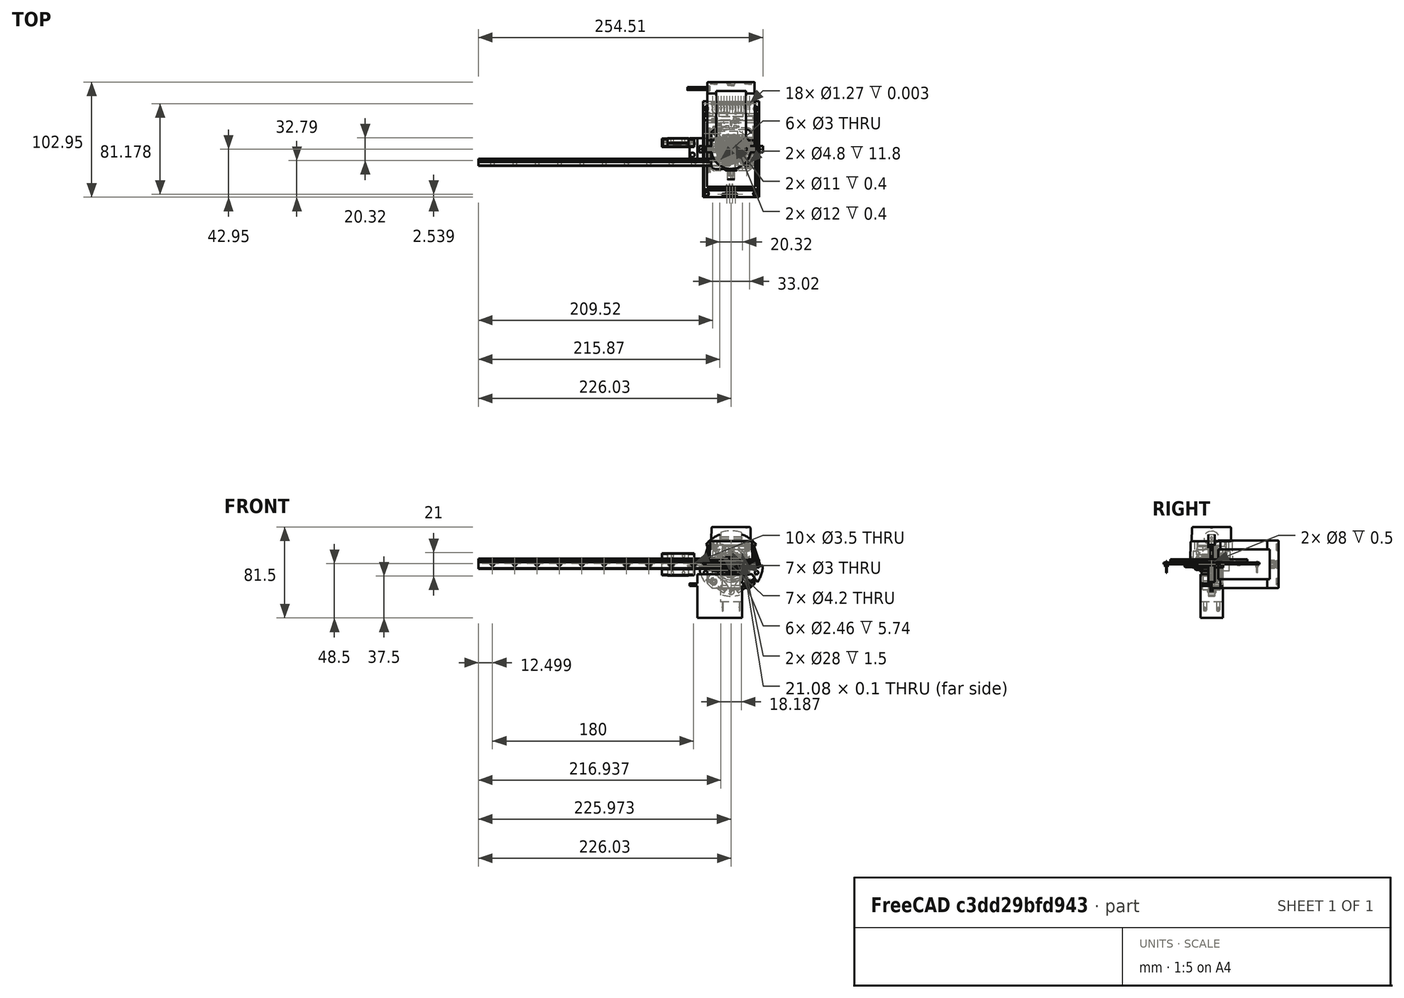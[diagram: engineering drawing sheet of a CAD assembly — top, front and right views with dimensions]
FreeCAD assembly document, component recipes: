
FREECAD ASSEMBLY — COMPONENT RECIPES ("generic-hardware")

This assembly document has 34 components, labeled P0..P33 below (a component is one placed body or linked part). 32 of them carry a construction recipe — the FreeCAD feature program that regenerates the part from scratch, quoted from this document or its linked companion documents; the rest are supplied as boundary geometry only. No exploded tour is included for this assembly.
NOTE — this tour is split across 3 documents so each fits a 32k-token context. This is document 1: the component sections continue in the remaining 2 documents, each repeating the header above.
COMPONENT P0 — recipe-attached ("Corner", modeled in this document).
Construction recipe (the document's own serialized feature program — sketch geometry with constraints, then the solid features built on it; lengths are millimeters unless a unit is written):

FEATURE [PartDesign::Plane] DatumPlane
  AttachmentOffset = pos=(0,0,5) rot=(0,0,1;0rad)
  FixShape = 1
  InvalidShape = false
  Length = 10
  MapMode = 5
  MinimumLength = 10
  MinimumWidth = 10
  Placement = pos=(5,0,0) rot=(0.57735,0.57735,0.57735;2.0944rad)
  ResizeMode = 0
  TreeRank = 0
  ValidateShape = false
  Width = 10
FEATURE [PartDesign::PolarPattern] PolarPattern
  AddSubType = 0
  Angle = 90
  Axis = -> Z_Axis001
  CopyShape = true
  FixShape = 1
  InvalidShape = false
  NewSolid = false
  Occurrences = 2
  ParallelTransform = true
  Placement = pos=(0,0,0) rot=(0.57735,0.57735,0.57735;2.0944rad)
  Refine = true
  SubTransform = true
  Suppress = false
  TreeRank = 0
  ValidateShape = true
  _Version = 0
FEATURE [PartDesign::PolarPattern] PolarPattern001
  AddSubType = 0
  Angle = 90
  Axis = -> Y_Axis001
  CopyShape = true
  FixShape = 1
  InvalidShape = false
  NewSolid = false
  Occurrences = 2
  ParallelTransform = true
  Placement = pos=(0,0,0) rot=(0.57735,0.57735,0.57735;2.0944rad)
  Refine = true
  SubTransform = true
  Suppress = false
  TreeRank = 0
  ValidateShape = true
  _Version = 0
FEATURE [PartDesign::PolarPattern] PolarPattern002
  AddSubType = 0
  Angle = 90
  Axis = -> Y_Axis001
  CopyShape = true
  FixShape = 1
  InvalidShape = false
  NewSolid = false
  Occurrences = 2
  ParallelTransform = true
  Placement = pos=(0,0,0) rot=(0.57735,0.57735,0.57735;2.0944rad)
  Refine = true
  SubTransform = true
  Suppress = false
  TreeRank = 0
  ValidateShape = true
  _Version = 0
FEATURE [PartDesign::PolarPattern] PolarPattern003
  AddSubType = 0
  Angle = 90
  Axis = -> Z_Axis001
  CopyShape = true
  FixShape = 1
  InvalidShape = false
  NewSolid = false
  Occurrences = 2
  ParallelTransform = true
  Placement = pos=(0,0,0) rot=(0.57735,0.57735,0.57735;2.0944rad)
  Refine = true
  SubTransform = true
  Suppress = false
  TreeRank = 0
  ValidateShape = true
  _Version = 0
FEATURE [Sketcher::SketchObject] Sketch207
  ArcFitTolerance = 0
  ExternalBSplineMaxDegree = 0
  ExternalBSplineTolerance = 0
  FixShape = 1
  FullyConstrained = true
  InternalTolerance = 1e-06
  InvalidShape = false
  MakeInternals = false
  MapMode = 5
  Placement = pos=(0,0,0) rot=(0.57735,0.57735,0.57735;2.0944rad)
  TreeRank = 0
  ValidateShape = false
  sketch-geometry (4):
    g0: LineSegment StartX=-5 StartY=5 StartZ=0 EndX=5 EndY=5 EndZ=0
    g1: LineSegment StartX=5 StartY=5 StartZ=0 EndX=5 EndY=-5 EndZ=0
    g2: LineSegment StartX=5 StartY=-5 StartZ=0 EndX=-5 EndY=-5 EndZ=0
    g3: LineSegment StartX=-5 StartY=-5 StartZ=0 EndX=-5 EndY=5 EndZ=0
  constraints (11):
    c: Coincident(g0,g1)
    c: Coincident(g1,g2)
    c: Coincident(g2,g3)
    c: Coincident(g3,g0)
    c: Horizontal(g0)
    c: Horizontal(g2)
    c: Vertical(g1)
    c: Vertical(g3)
    c: Symmetric(g1,g0,g-1)
    c: Equal(g0,g3)
    c: DistanceX(g0,g0) = 10
FEATURE [PartDesign::Pad] Pad084
  AddSubType = 0
  AutoTaperInnerAngle = true
  CheckUpToFaceLimits = true
  ClaimChildren = false
  Direction = (1,1e-16,-1e-16)
  Fit = 0
  FitJoin = 0
  FixShape = 1
  InnerFit = 0
  InnerFitJoin = 0
  InvalidShape = false
  Length = 10
  Length2 = 100
  Midplane = true
  NewSolid = false
  Placement = pos=(0,0,0) rot=(0.57735,0.57735,0.57735;2.0944rad)
  Profile = -> Sketch207
  Refine = true
  Suppress = false
  TaperInnerAngle = 0
  TaperInnerAngleRev = 0
  TreeRank = 0
  Type = 0
  ValidateShape = true
  _ProfileBasedVersion = 0
FEATURE [Sketcher::SketchObject] Sketch208
  ArcFitTolerance = 0
  ExternalBSplineMaxDegree = 0
  ExternalBSplineTolerance = 0
  FixShape = 1
  FullyConstrained = true
  InternalTolerance = 1e-06
  InvalidShape = false
  MakeInternals = false
  MapMode = 5
  Placement = pos=(0,0,0) rot=(0.57735,0.57735,0.57735;2.0944rad)
  TreeRank = 0
  ValidateShape = false
  sketch-geometry (1):
    g0: Circle CenterX=0 CenterY=0 CenterZ=0 NormalX=0 NormalY=0 NormalZ=1 AngleXU=0 Radius=1.5
  constraints (2):
    c: Coincident(g0,g-1)
    c: Diameter(g0) = 3
FEATURE [PartDesign::Pocket] Pocket039
  AddSubType = 1
  AutoTaperInnerAngle = true
  BaseFeature = -> Pad084
  CheckUpToFaceLimits = true
  ClaimChildren = false
  Direction = (-1,-1e-16,1e-16)
  Fit = 0
  FitJoin = 0
  FixShape = 1
  InnerFit = 0
  InnerFitJoin = 0
  InvalidShape = false
  Length = 5
  Length2 = 100
  Midplane = true
  NewSolid = false
  Placement = pos=(0,0,0) rot=(0.57735,0.57735,0.57735;2.0944rad)
  Profile = -> Sketch208
  Refine = true
  Suppress = false
  TaperInnerAngle = 0
  TaperInnerAngleRev = 0
  TreeRank = 0
  Type = 1
  ValidateShape = true
  _ProfileBasedVersion = 0
  _Version = 0
FEATURE [PartDesign::MultiTransform] MultiTransform
  AddSubType = 0
  BaseFeature = -> Pocket039
  CopyShape = true
  FixShape = 1
  InvalidShape = false
  NewSolid = false
  OriginalSubs = -> [Pocket039]
  Originals = -> [Pocket039]
  ParallelTransform = true
  Placement = pos=(0,0,0) rot=(0.57735,0.57735,0.57735;2.0944rad)
  Refine = true
  SubTransform = true
  Suppress = false
  Transformations = -> [PolarPattern,PolarPattern001]
  TreeRank = 0
  ValidateShape = true
  _Version = 0
FEATURE [Sketcher::SketchObject] Sketch209
  ArcFitTolerance = 0
  ExternalBSplineMaxDegree = 0
  ExternalBSplineTolerance = 0
  FixShape = 1
  FullyConstrained = true
  InternalTolerance = 1e-06
  InvalidShape = false
  MakeInternals = false
  MapMode = 5
  Placement = pos=(5,0,0) rot=(0.57735,0.57735,0.57735;2.0944rad)
  TreeRank = 0
  ValidateShape = false
  sketch-geometry (1):
    g0: Circle CenterX=0 CenterY=0 CenterZ=0 NormalX=0 NormalY=0 NormalZ=1 AngleXU=0 Radius=3
  constraints (2):
    c: Coincident(g0,g-1)
    c: Diameter(g0) = 6
FEATURE [PartDesign::Pocket] Pocket040
  AddSubType = 1
  AutoTaperInnerAngle = true
  BaseFeature = -> MultiTransform
  CheckUpToFaceLimits = true
  ClaimChildren = false
  Direction = (-1,-1e-16,1e-16)
  Fit = 0
  FitJoin = 0
  FixShape = 1
  InnerFit = 0
  InnerFitJoin = 0
  InvalidShape = false
  Length = 8
  Length2 = 100
  NewSolid = false
  Placement = pos=(0,0,0) rot=(0.57735,0.57735,0.57735;2.0944rad)
  Profile = -> Sketch209
  Refine = true
  Suppress = false
  TaperInnerAngle = 0
  TaperInnerAngleRev = 0
  TreeRank = 0
  Type = 0
  ValidateShape = true
  _ProfileBasedVersion = 0
  _Version = 0
FEATURE [PartDesign::MultiTransform] MultiTransform001
  AddSubType = 0
  BaseFeature = -> Pocket040
  CopyShape = true
  FixShape = 1
  InvalidShape = false
  NewSolid = false
  OriginalSubs = -> [Pocket040]
  Originals = -> [Pocket040]
  ParallelTransform = true
  Placement = pos=(0,0,0) rot=(0.57735,0.57735,0.57735;2.0944rad)
  Refine = true
  SubTransform = true
  Suppress = false
  Transformations = -> [PolarPattern002,PolarPattern003]
  TreeRank = 0
  ValidateShape = true
  _Version = 0
FEATURE [PartDesign::Body] Body001  label="Corner"
  AutoGroupSolids = false
  ClaimAllChildren = false
  ExportMode = 0
  FixShape = 1
  Group = -> [Sketch207,Pad084,Sketch208,Pocket039,MultiTransform,PolarPattern,PolarPattern001,DatumPlane,Sketch209,Pocket040,MultiTransform001,PolarPattern002,PolarPattern003]
  InvalidShape = false
  Origin = -> Origin001
  SingleSolid = true
  Tip = -> MultiTransform001
  TreeRank = 0
  ValidateShape = false
  _ExportChildren = -> [Pad084,Pocket039,MultiTransform,DatumPlane,Pocket040,MultiTransform001]
  _GroupVersion = 1
COMPONENT P1 — recipe-attached ("MB_100", modeled in this document).
Construction recipe (the document's own serialized feature program — sketch geometry with constraints, then the solid features built on it; lengths are millimeters unless a unit is written):

FEATURE [PartDesign::CoordinateSystem] Local_CS
  AttacherType = Attacher::AttachEngine3D
  FixShape = 1
  InvalidShape = false
  Placement = pos=(4.4e-14,100,0) rot=(1,0,0;1.5708rad)
  TreeRank = 0
  ValidateShape = false
FEATURE [Sketcher::SketchObject] Sketch206
  ArcFitTolerance = 0
  ExternalBSplineMaxDegree = 0
  ExternalBSplineTolerance = 0
  FixShape = 1
  FullyConstrained = true
  InternalTolerance = 1e-06
  InvalidShape = false
  MakeInternals = false
  MapMode = 5
  Placement = pos=(0,0,0) rot=(1,0,0;1.5708rad)
  TreeRank = 0
  ValidateShape = false
  sketch-geometry (14):
    g0: ArcOfCircle CenterX=0 CenterY=0 CenterZ=0 NormalX=0 NormalY=0 NormalZ=1 AngleXU=0 Radius=1.25 StartAngle=0 EndAngle=1.5708
    g1: LineSegment StartX=1e-16 StartY=1.25 StartZ=0 EndX=0 EndY=2 EndZ=0
    g2: LineSegment StartX=0 StartY=2 StartZ=0 EndX=1 EndY=2 EndZ=0
    g3: LineSegment [constr] StartX=0 StartY=0 StartZ=0 EndX=5 EndY=5 EndZ=0
    g4: LineSegment StartX=1 StartY=2 StartZ=0 EndX=3.3 EndY=4 EndZ=0
    g5: LineSegment StartX=3.3 StartY=4 StartZ=0 EndX=1.5 EndY=4 EndZ=0
    g6: LineSegment StartX=1.5 StartY=4 StartZ=0 EndX=1.5 EndY=5 EndZ=0
    g7: LineSegment StartX=1.5 StartY=5 StartZ=0 EndX=5 EndY=5 EndZ=0
    g8: LineSegment StartX=5 StartY=5 StartZ=0 EndX=5 EndY=1.5 EndZ=0
    g9: LineSegment StartX=5 StartY=1.5 StartZ=0 EndX=4 EndY=1.5 EndZ=0
    g10: LineSegment StartX=4 StartY=1.5 StartZ=0 EndX=4 EndY=3.3 EndZ=0
    g11: LineSegment StartX=4 StartY=3.3 StartZ=0 EndX=2 EndY=1 EndZ=0
    g12: LineSegment StartX=2 StartY=1 StartZ=0 EndX=2 EndY=0 EndZ=0
    g13: LineSegment StartX=2 StartY=0 StartZ=0 EndX=1.25 EndY=0 EndZ=0
  constraints (41):
    c: Coincident(g0,g-1)
    c: PointOnObject(g0,g-1)
    c: PointOnObject(g0,g-2)
    c: Coincident(g1,g0)
    c: PointOnObject(g1,g-2)
    c: Coincident(g2,g1)
    c: Horizontal(g2)
    c: Coincident(g3,g0)
    c: Angle(g-1,g3) = 0.785398
    c: DistanceX(g3) = 5
    c: Diameter(g0) = 2.5
    c: DistanceX(g2) = 1
    c: Coincident(g4,g2)
    c: Coincident(g5,g4)
    c: Horizontal(g5)
    c: Coincident(g6,g5)
    c: Vertical(g6)
    c: Coincident(g7,g6)
    c: Coincident(g7,g3)
    c: Coincident(g8,g7)
    c: Vertical(g8)
    c: Coincident(g9,g8)
    c: Coincident(g10,g9)
    c: Vertical(g10)
    c: Coincident(g11,g10)
    c: Coincident(g12,g11)
    c: PointOnObject(g12,g-1)
    c: Vertical(g12)
    c: Coincident(g13,g12)
    c: Coincident(g13,g0)
    c: Equal(g12,g2)
    c: Equal(g13,g1)
    c: Horizontal(g7)
    c: Horizontal(g9)
    c: Equal(g6,g9)
    c: Equal(g11,g4)
    c: Equal(g5,g10)
    c: DistanceY(g2,g6) = 3
    c: DistanceX(g6) = 1.5
    c: DistanceY(g6,g6) = 1
    c: DistanceX(g5,g5) = 1.8
FEATURE [PartDesign::Pad] Pad083
  AddSubType = 0
  AutoTaperInnerAngle = true
  CheckUpToFaceLimits = true
  ClaimChildren = false
  Direction = (0,-1,0)
  Fit = 0
  FitJoin = 0
  FixShape = 1
  InnerFit = 0
  InnerFitJoin = 0
  InvalidShape = false
  Length = 100
  Length2 = 100
  NewSolid = false
  Placement = pos=(0,0,0) rot=(1,0,0;1.5708rad)
  Profile = -> Sketch206
  Refine = true
  Reversed = true
  Suppress = false
  TaperInnerAngle = 0
  TaperInnerAngleRev = 0
  TreeRank = 0
  Type = 0
  ValidateShape = true
  _ProfileBasedVersion = 0
FEATURE [PartDesign::PolarPattern] PolarPattern004
  AddSubType = 0
  Angle = 360
  Axis = -> Y_Axis002
  BaseFeature = -> Pad083
  CopyShape = true
  FixShape = 1
  InvalidShape = false
  NewSolid = false
  Occurrences = 4
  OriginalSubs = -> [Pad083]
  Originals = -> [Pad083]
  ParallelTransform = true
  Placement = pos=(0,0,0) rot=(1,0,0;1.5708rad)
  Refine = true
  SubTransform = true
  Suppress = false
  TreeRank = 0
  ValidateShape = true
  _Version = 0
FEATURE [PartDesign::Body] Body002  label="MB_100"
  AutoGroupSolids = false
  ClaimAllChildren = false
  ExportMode = 0
  FixShape = 1
  Group = -> [Sketch206,Pad083,PolarPattern004,Local_CS]
  InvalidShape = false
  Origin = -> Origin002
  SingleSolid = true
  Tip = -> PolarPattern004
  TreeRank = 0
  ValidateShape = false
  _ExportChildren = -> [Pad083,PolarPattern004,Local_CS]
  _GroupVersion = 1
COMPONENT P2 — recipe-attached ("MB_60", modeled in this document).
Construction recipe (the document's own serialized feature program — sketch geometry with constraints, then the solid features built on it; lengths are millimeters unless a unit is written):

FEATURE [Sketcher::SketchObject] Sketch005
  ArcFitTolerance = 0
  ExternalBSplineMaxDegree = 0
  ExternalBSplineTolerance = 0
  FixShape = 1
  FullyConstrained = true
  InternalTolerance = 1e-06
  InvalidShape = false
  MakeInternals = false
  MapMode = 5
  Placement = pos=(0,0,0) rot=(1,0,0;1.5708rad)
  TreeRank = 0
  ValidateShape = false
  sketch-geometry (14):
    g0: ArcOfCircle CenterX=0 CenterY=0 CenterZ=0 NormalX=0 NormalY=0 NormalZ=1 AngleXU=0 Radius=1.25 StartAngle=0 EndAngle=1.5708
    g1: LineSegment StartX=1e-16 StartY=1.25 StartZ=0 EndX=0 EndY=2 EndZ=0
    g2: LineSegment StartX=0 StartY=2 StartZ=0 EndX=1 EndY=2 EndZ=0
    g3: LineSegment [constr] StartX=0 StartY=0 StartZ=0 EndX=5 EndY=5 EndZ=0
    g4: LineSegment StartX=1 StartY=2 StartZ=0 EndX=3.3 EndY=4 EndZ=0
    g5: LineSegment StartX=3.3 StartY=4 StartZ=0 EndX=1.5 EndY=4 EndZ=0
    g6: LineSegment StartX=1.5 StartY=4 StartZ=0 EndX=1.5 EndY=5 EndZ=0
    g7: LineSegment StartX=1.5 StartY=5 StartZ=0 EndX=5 EndY=5 EndZ=0
    g8: LineSegment StartX=5 StartY=5 StartZ=0 EndX=5 EndY=1.5 EndZ=0
    g9: LineSegment StartX=5 StartY=1.5 StartZ=0 EndX=4 EndY=1.5 EndZ=0
    g10: LineSegment StartX=4 StartY=1.5 StartZ=0 EndX=4 EndY=3.3 EndZ=0
    g11: LineSegment StartX=4 StartY=3.3 StartZ=0 EndX=2 EndY=1 EndZ=0
    g12: LineSegment StartX=2 StartY=1 StartZ=0 EndX=2 EndY=0 EndZ=0
    g13: LineSegment StartX=2 StartY=0 StartZ=0 EndX=1.25 EndY=0 EndZ=0
  constraints (41):
    c: Coincident(g0,g-1)
    c: PointOnObject(g0,g-1)
    c: PointOnObject(g0,g-2)
    c: Coincident(g1,g0)
    c: PointOnObject(g1,g-2)
    c: Coincident(g2,g1)
    c: Horizontal(g2)
    c: Coincident(g3,g0)
    c: Angle(g-1,g3) = 0.785398
    c: DistanceX(g3) = 5
    c: Diameter(g0) = 2.5
    c: DistanceX(g2) = 1
    c: Coincident(g4,g2)
    c: Coincident(g5,g4)
    c: Horizontal(g5)
    c: Coincident(g6,g5)
    c: Vertical(g6)
    c: Coincident(g7,g6)
    c: Coincident(g7,g3)
    c: Coincident(g8,g7)
    c: Vertical(g8)
    c: Coincident(g9,g8)
    c: Coincident(g10,g9)
    c: Vertical(g10)
    c: Coincident(g11,g10)
    c: Coincident(g12,g11)
    c: PointOnObject(g12,g-1)
    c: Vertical(g12)
    c: Coincident(g13,g12)
    c: Coincident(g13,g0)
    c: Equal(g12,g2)
    c: Equal(g13,g1)
    c: Horizontal(g7)
    c: Horizontal(g9)
    c: Equal(g6,g9)
    c: Equal(g11,g4)
    c: Equal(g5,g10)
    c: DistanceY(g2,g6) = 3
    c: DistanceX(g6) = 1.5
    c: DistanceY(g6,g6) = 1
    c: DistanceX(g5,g5) = 1.8
FEATURE [PartDesign::Pad] Pad003
  AddSubType = 0
  AutoTaperInnerAngle = true
  CheckUpToFaceLimits = true
  ClaimChildren = false
  Direction = (0,-1,0)
  Fit = 0
  FitJoin = 0
  FixShape = 1
  InnerFit = 0
  InnerFitJoin = 0
  InvalidShape = false
  Length = 60
  Length2 = 100
  NewSolid = false
  Placement = pos=(0,0,0) rot=(1,0,0;1.5708rad)
  Profile = -> Sketch005
  Refine = true
  Reversed = true
  Suppress = false
  TaperInnerAngle = 0
  TaperInnerAngleRev = 0
  TreeRank = 0
  Type = 0
  ValidateShape = true
  _ProfileBasedVersion = 0
FEATURE [PartDesign::PolarPattern] PolarPattern005
  AddSubType = 0
  Angle = 360
  AttacherType = Attacher::AttachEngine3D
  Axis = -> Y_Axis003
  BaseFeature = -> Pad003
  CopyShape = true
  FixShape = 1
  InvalidShape = false
  NewSolid = false
  Occurrences = 4
  OriginalSubs = -> [Pad003]
  Originals = -> [Pad003]
  ParallelTransform = true
  Placement = pos=(0,0,0) rot=(1,0,0;1.5708rad)
  Refine = true
  SubTransform = true
  Suppress = false
  TreeRank = 0
  ValidateShape = true
  _Version = 0
FEATURE [PartDesign::Body] Body003  label="MB_60"
  AutoGroupSolids = false
  ClaimAllChildren = false
  ExportMode = 0
  FixShape = 1
  Group = -> [Sketch005,Pad003,PolarPattern005]
  InvalidShape = false
  Origin = -> Origin003
  SingleSolid = true
  Tip = -> PolarPattern005
  TreeRank = 0
  ValidateShape = false
  _ExportChildren = -> [Pad003,PolarPattern005]
  _GroupVersion = 1
COMPONENT P3 — recipe-attached ("MB_300", modeled in this document).
Construction recipe (the document's own serialized feature program — sketch geometry with constraints, then the solid features built on it; lengths are millimeters unless a unit is written):

FEATURE [Sketcher::SketchObject] Sketch006
  ArcFitTolerance = 0
  ExternalBSplineMaxDegree = 0
  ExternalBSplineTolerance = 0
  FixShape = 1
  FullyConstrained = true
  InternalTolerance = 1e-06
  InvalidShape = false
  MakeInternals = false
  MapMode = 5
  Placement = pos=(0,0,0) rot=(1,0,0;1.5708rad)
  TreeRank = 0
  ValidateShape = false
  sketch-geometry (14):
    g0: ArcOfCircle CenterX=0 CenterY=0 CenterZ=0 NormalX=0 NormalY=0 NormalZ=1 AngleXU=0 Radius=1.25 StartAngle=0 EndAngle=1.5708
    g1: LineSegment StartX=1e-16 StartY=1.25 StartZ=0 EndX=0 EndY=2 EndZ=0
    g2: LineSegment StartX=0 StartY=2 StartZ=0 EndX=1 EndY=2 EndZ=0
    g3: LineSegment [constr] StartX=0 StartY=0 StartZ=0 EndX=5 EndY=5 EndZ=0
    g4: LineSegment StartX=1 StartY=2 StartZ=0 EndX=3.3 EndY=4 EndZ=0
    g5: LineSegment StartX=3.3 StartY=4 StartZ=0 EndX=1.5 EndY=4 EndZ=0
    g6: LineSegment StartX=1.5 StartY=4 StartZ=0 EndX=1.5 EndY=5 EndZ=0
    g7: LineSegment StartX=1.5 StartY=5 StartZ=0 EndX=5 EndY=5 EndZ=0
    g8: LineSegment StartX=5 StartY=5 StartZ=0 EndX=5 EndY=1.5 EndZ=0
    g9: LineSegment StartX=5 StartY=1.5 StartZ=0 EndX=4 EndY=1.5 EndZ=0
    g10: LineSegment StartX=4 StartY=1.5 StartZ=0 EndX=4 EndY=3.3 EndZ=0
    g11: LineSegment StartX=4 StartY=3.3 StartZ=0 EndX=2 EndY=1 EndZ=0
    g12: LineSegment StartX=2 StartY=1 StartZ=0 EndX=2 EndY=0 EndZ=0
    g13: LineSegment StartX=2 StartY=0 StartZ=0 EndX=1.25 EndY=0 EndZ=0
  constraints (41):
    c: Coincident(g0,g-1)
    c: PointOnObject(g0,g-1)
    c: PointOnObject(g0,g-2)
    c: Coincident(g1,g0)
    c: PointOnObject(g1,g-2)
    c: Coincident(g2,g1)
    c: Horizontal(g2)
    c: Coincident(g3,g0)
    c: Angle(g-1,g3) = 0.785398
    c: DistanceX(g3) = 5
    c: Diameter(g0) = 2.5
    c: DistanceX(g2) = 1
    c: Coincident(g4,g2)
    c: Coincident(g5,g4)
    c: Horizontal(g5)
    c: Coincident(g6,g5)
    c: Vertical(g6)
    c: Coincident(g7,g6)
    c: Coincident(g7,g3)
    c: Coincident(g8,g7)
    c: Vertical(g8)
    c: Coincident(g9,g8)
    c: Coincident(g10,g9)
    c: Vertical(g10)
    c: Coincident(g11,g10)
    c: Coincident(g12,g11)
    c: PointOnObject(g12,g-1)
    c: Vertical(g12)
    c: Coincident(g13,g12)
    c: Coincident(g13,g0)
    c: Equal(g12,g2)
    c: Equal(g13,g1)
    c: Horizontal(g7)
    c: Horizontal(g9)
    c: Equal(g6,g9)
    c: Equal(g11,g4)
    c: Equal(g5,g10)
    c: DistanceY(g2,g6) = 3
    c: DistanceX(g6) = 1.5
    c: DistanceY(g6,g6) = 1
    c: DistanceX(g5,g5) = 1.8
FEATURE [PartDesign::Pad] Pad004
  AddSubType = 0
  AutoTaperInnerAngle = true
  CheckUpToFaceLimits = true
  ClaimChildren = false
  Direction = (0,-1,0)
  Fit = 0
  FitJoin = 0
  FixShape = 1
  InnerFit = 0
  InnerFitJoin = 0
  InvalidShape = false
  Length = 300
  Length2 = 100
  NewSolid = false
  Placement = pos=(0,0,0) rot=(1,0,0;1.5708rad)
  Profile = -> Sketch006
  Refine = true
  Reversed = true
  Suppress = false
  TaperInnerAngle = 0
  TaperInnerAngleRev = 0
  TreeRank = 0
  Type = 0
  ValidateShape = true
  _ProfileBasedVersion = 0
FEATURE [PartDesign::PolarPattern] PolarPattern006
  AddSubType = 0
  Angle = 360
  Axis = -> Y_Axis004
  BaseFeature = -> Pad004
  CopyShape = true
  FixShape = 1
  InvalidShape = false
  NewSolid = false
  Occurrences = 4
  OriginalSubs = -> [Pad004]
  Originals = -> [Pad004]
  ParallelTransform = true
  Placement = pos=(0,0,0) rot=(1,0,0;1.5708rad)
  Refine = true
  SubTransform = true
  Suppress = false
  TreeRank = 0
  ValidateShape = true
  _Version = 0
FEATURE [PartDesign::Body] Body004  label="MB_300"
  AutoGroupSolids = false
  ClaimAllChildren = false
  ExportMode = 0
  FixShape = 1
  Group = -> [Sketch006,Pad004,PolarPattern006]
  InvalidShape = false
  Origin = -> Origin004
  SingleSolid = true
  Tip = -> PolarPattern006
  TreeRank = 0
  ValidateShape = false
  _ExportChildren = -> [Pad004,PolarPattern006]
  _GroupVersion = 1
COMPONENT P4 — recipe-attached ("Gens ACE - 6S - 1250mAh + Bag", modeled in this document).
Construction recipe (the document's own serialized feature program — sketch geometry with constraints, then the solid features built on it; lengths are millimeters unless a unit is written):

FEATURE [Sketcher::SketchObject] Sketch025
  ArcFitTolerance = 0
  ExternalBSplineMaxDegree = 0
  ExternalBSplineTolerance = 0
  FixShape = 1
  FullyConstrained = true
  InternalTolerance = 1e-06
  InvalidShape = false
  MakeInternals = false
  MapMode = 5
  TreeRank = 0
  ValidateShape = false
  sketch-geometry (5):
    g0: LineSegment StartX=-22.5 StartY=-32.5 StartZ=0 EndX=-22.5 EndY=32.5 EndZ=0
    g1: LineSegment StartX=-22.5 StartY=32.5 StartZ=0 EndX=22.5 EndY=32.5 EndZ=0
    g2: LineSegment StartX=22.5 StartY=32.5 StartZ=0 EndX=22.5 EndY=-32.5 EndZ=0
    g3: LineSegment StartX=22.5 StartY=-32.5 StartZ=0 EndX=-22.5 EndY=-32.5 EndZ=0
    g4: GeomPoint [constr] X=0 Y=0 Z=0
  constraints (12):
    c: Coincident(g0,g1)
    c: Coincident(g1,g2)
    c: Coincident(g2,g3)
    c: Coincident(g3,g0)
    c: Horizontal(g1)
    c: Horizontal(g3)
    c: Vertical(g0)
    c: Vertical(g2)
    c: Symmetric(g1,g0,g4)
    c: Coincident(g4,g-1)
    c: DistanceY(g0,g0) = 65
    c: DistanceX(g1,g1) = 45
FEATURE [PartDesign::Pad] Pad010
  AddSubType = 0
  AlongSketchNormal = false
  AutoTaperInnerAngle = true
  CheckUpToFaceLimits = true
  ClaimChildren = false
  Direction = (0,0,1)
  Fit = 0
  FitJoin = 0
  FixShape = 1
  InnerFit = 0
  InnerFitJoin = 0
  InvalidShape = false
  Length = 110
  Length2 = 10
  NewSolid = false
  Profile = -> Sketch025
  ReferenceAxis = -> Sketch025 [N_Axis]
  Refine = true
  Suppress = false
  TaperInnerAngle = 0
  TaperInnerAngleRev = 0
  TreeRank = 0
  Type = 0
  ValidateShape = true
  _ProfileBasedVersion = 0
FEATURE [PartDesign::Fillet] Fillet009
  AddSubType = 0
  Base = -> Pad010 [Edge4,Edge10]
  BaseFeature = -> Pad010
  FixShape = 1
  InvalidShape = false
  NewSolid = false
  Radius = 6
  Refine = true
  SupportTransform = false
  Suppress = false
  TreeRank = 0
  UseAllEdges = false
  ValidateShape = true
FEATURE [Sketcher::SketchObject] Sketch026
  ArcFitTolerance = 0
  AttachmentSupport = -> [Fillet009]
  ExternalBSplineMaxDegree = 0
  ExternalBSplineTolerance = 0
  ExternalGeometry = -> [Fillet009]
  FixShape = 1
  FullyConstrained = true
  InternalTolerance = 1e-06
  InvalidShape = false
  MakeInternals = false
  MapMode = 5
  Placement = pos=(0,-32.5,0) rot=(1,0,0;1.5708rad)
  Support = -> [Fillet009]
  TreeRank = 0
  ValidateShape = false
  sketch-geometry (4):
    g0: LineSegment StartX=17.5 StartY=105 StartZ=0 EndX=-12.5 EndY=105 EndZ=0
    g1: LineSegment StartX=-12.5 StartY=105 StartZ=0 EndX=-12.5 EndY=13 EndZ=0
    g2: LineSegment StartX=-12.5 StartY=13 StartZ=0 EndX=17.5 EndY=13 EndZ=0
    g3: LineSegment StartX=17.5 StartY=13 StartZ=0 EndX=17.5 EndY=105 EndZ=0
  constraints (12):
    c: Coincident(g0,g1)
    c: Coincident(g1,g2)
    c: Coincident(g2,g3)
    c: Coincident(g3,g0)
    c: Horizontal(g0)
    c: Horizontal(g2)
    c: Vertical(g1)
    c: Vertical(g3)
    c: DistanceX(g0,g-3) = 5
    c: DistanceX(g0,g0) = 30
    c: DistanceY(g-3,g2) = 13
    c: DistanceY(g0,g-4) = 5
FEATURE [PartDesign::Pocket] Pocket013
  AddSubType = 1
  AlongSketchNormal = false
  AutoTaperInnerAngle = true
  BaseFeature = -> Fillet009
  CheckUpToFaceLimits = true
  ClaimChildren = false
  Direction = (0,1,-2e-16)
  Fit = 0
  FitJoin = 0
  FixShape = 1
  InnerFit = 0
  InnerFitJoin = 0
  InvalidShape = false
  Length = 12
  Length2 = 10
  NewSolid = false
  Profile = -> Sketch026
  ReferenceAxis = -> Sketch026 [N_Axis]
  Refine = true
  Suppress = false
  TaperInnerAngle = 0
  TaperInnerAngleRev = 0
  TreeRank = 0
  Type = 0
  ValidateShape = true
  _ProfileBasedVersion = 0
  _Version = 0
FEATURE [PartDesign::Mirrored] Mirrored001
  AddSubType = 0
  BaseFeature = -> Pocket013
  CopyShape = true
  FixShape = 1
  InvalidShape = false
  MirrorPlane = -> XZ_Plane011
  NewSolid = false
  OriginalSubs = -> [Pocket013]
  Originals = -> [Pocket013]
  ParallelTransform = true
  Refine = true
  SubTransform = true
  Suppress = false
  TreeRank = 0
  ValidateShape = true
  _Version = 0
FEATURE [Sketcher::SketchObject] Sketch027
  ArcFitTolerance = 0
  AttachmentSupport = -> [Mirrored001]
  ExternalBSplineMaxDegree = 0
  ExternalBSplineTolerance = 0
  ExternalGeometry = -> [Mirrored001]
  FixShape = 1
  FullyConstrained = false
  InternalTolerance = 1e-06
  InvalidShape = false
  MakeInternals = false
  MapMode = 5
  Placement = pos=(0,-20.5,4.7e-15) rot=(1,0,0;1.5708rad)
  Support = -> [Mirrored001]
  TreeRank = 0
  ValidateShape = false
  sketch-geometry (3):
    g0: Circle CenterX=-5 CenterY=101 CenterZ=0 NormalX=0 NormalY=0 NormalZ=1 AngleXU=0 Radius=2
    g1: Circle CenterX=10 CenterY=101 CenterZ=0 NormalX=0 NormalY=0 NormalZ=1 AngleXU=0 Radius=2
    g2: LineSegment [constr] StartX=2.5 StartY=105 StartZ=0 EndX=2.5 EndY=91.3759 EndZ=0
  constraints (7):
    c: Equal(g1,g0)
    c: Diameter(g1) = 4
    c: Vertical(g2)
    c: Symmetric(g-3,g-3,g2)
    c: Symmetric(g0,g1,g2)
    c: DistanceX(g0,g1) = 15
    c: DistanceY(g1,g-3) = 4
FEATURE [PartDesign::Pad] Pad011
  AddSubType = 0
  AlongSketchNormal = false
  AutoTaperInnerAngle = true
  BaseFeature = -> Mirrored001
  CheckUpToFaceLimits = true
  ClaimChildren = false
  Direction = (0,-1,2e-16)
  Fit = 0
  FitJoin = 0
  FixShape = 1
  InnerFit = 0
  InnerFitJoin = 0
  InvalidShape = false
  Length = 10
  Length2 = 10
  NewSolid = false
  Profile = -> Sketch027
  ReferenceAxis = -> Sketch027 [N_Axis]
  Refine = true
  Suppress = false
  TaperInnerAngle = 0
  TaperInnerAngleRev = 0
  TreeRank = 0
  Type = 0
  ValidateShape = true
  _ProfileBasedVersion = 0
FEATURE [Sketcher::SketchObject] Sketch028
  ArcFitTolerance = 0
  AttachmentSupport = -> [Pad011]
  ExternalBSplineMaxDegree = 0
  ExternalBSplineTolerance = 0
  ExternalGeometry = -> [Pad011]
  FixShape = 1
  FullyConstrained = true
  InternalTolerance = 1e-06
  InvalidShape = false
  MakeInternals = false
  MapMode = 5
  Placement = pos=(-22.5,0,0) rot=(0.57735,-0.57735,-0.57735;2.0944rad)
  Support = -> [Pad011]
  TreeRank = 0
  ValidateShape = false
  sketch-geometry (4):
    g0: LineSegment StartX=-32.5 StartY=0 StartZ=0 EndX=32.5 EndY=0 EndZ=0
    g1: LineSegment StartX=32.5 StartY=0 StartZ=0 EndX=32.5 EndY=50 EndZ=0
    g2: LineSegment StartX=32.5 StartY=50 StartZ=0 EndX=-32.5 EndY=50 EndZ=0
    g3: LineSegment StartX=-32.5 StartY=50 StartZ=0 EndX=-32.5 EndY=0 EndZ=0
  constraints (11):
    c: Coincident(g0,g1)
    c: Coincident(g1,g2)
    c: Coincident(g2,g3)
    c: Coincident(g3,g0)
    c: Horizontal(g0)
    c: Horizontal(g2)
    c: Vertical(g1)
    c: Vertical(g3)
    c: Coincident(g0,g-3)
    c: PointOnObject(g1,g-4)
    c: DistanceY(g1,g-5) = 60
FEATURE [PartDesign::Pocket] Pocket014
  AddSubType = 1
  AlongSketchNormal = false
  AutoTaperInnerAngle = true
  BaseFeature = -> Pad011
  CheckUpToFaceLimits = true
  ClaimChildren = false
  Direction = (1,0,0)
  Fit = 0
  FitJoin = 0
  FixShape = 1
  InnerFit = 0
  InnerFitJoin = 0
  InvalidShape = false
  Length = 5
  Length2 = 10
  NewSolid = false
  Profile = -> Sketch028
  ReferenceAxis = -> Sketch028 [N_Axis]
  Refine = true
  Suppress = false
  TaperInnerAngle = 0
  TaperInnerAngleRev = 0
  TreeRank = 0
  Type = 0
  ValidateShape = true
  _ProfileBasedVersion = 0
  _Version = 0
FEATURE [PartDesign::Fillet] Fillet010
  AddSubType = 0
  Base = -> Pocket014 [Edge6,Edge5]
  BaseFeature = -> Pocket014
  FixShape = 1
  InvalidShape = false
  NewSolid = false
  Radius = 20
  Refine = true
  SupportTransform = false
  Suppress = false
  TreeRank = 0
  UseAllEdges = false
  ValidateShape = true
FEATURE [PartDesign::Fillet] Fillet011
  AddSubType = 0
  Base = -> Fillet010 [Edge37,Edge40]
  BaseFeature = -> Fillet010
  FixShape = 1
  InvalidShape = false
  NewSolid = false
  Radius = 3
  Refine = true
  SupportTransform = false
  Suppress = false
  TreeRank = 0
  UseAllEdges = false
  ValidateShape = true
FEATURE [PartDesign::Body] Body011  label="Gens ACE - 6S - 1250mAh + Bag"
  AutoGroupSolids = false
  ClaimAllChildren = false
  ExportMode = 0
  FixShape = 1
  Group = -> [Sketch025,Pad010,Fillet009,Sketch026,Pocket013,Mirrored001,Sketch027,Pad011,Sketch028,Pocket014,Fillet010,Fillet011]
  InvalidShape = false
  Origin = -> Origin198
  SingleSolid = true
  Tip = -> Fillet011
  TreeRank = 0
  ValidateShape = false
  _ExportChildren = -> [Pad010,Fillet009,Pocket013,Mirrored001,Pad011,Pocket014,Fillet010,Fillet011]
  _GroupVersion = 1
COMPONENT P5 — recipe-attached ("RoundServoHorn", modeled in this document).
Construction recipe (the document's own serialized feature program — sketch geometry with constraints, then the solid features built on it; lengths are millimeters unless a unit is written):

FEATURE [Sketcher::SketchObject] Sketch088
  ArcFitTolerance = 0
  ExternalBSplineMaxDegree = 0
  ExternalBSplineTolerance = 0
  FixShape = 1
  FullyConstrained = true
  InternalTolerance = 1e-06
  InvalidShape = false
  MakeInternals = false
  MapMode = 5
  TreeRank = 0
  ValidateShape = false
  sketch-geometry (7):
    g0: Circle CenterX=0 CenterY=0 CenterZ=0 NormalX=0 NormalY=0 NormalZ=1 AngleXU=0 Radius=10
    g1: Circle CenterX=0 CenterY=7 CenterZ=0 NormalX=0 NormalY=0 NormalZ=1 AngleXU=0 Radius=1.5
    g2: Circle CenterX=7 CenterY=0 CenterZ=0 NormalX=0 NormalY=0 NormalZ=1 AngleXU=0 Radius=1.5
    g3: Circle CenterX=0 CenterY=-7 CenterZ=0 NormalX=0 NormalY=0 NormalZ=1 AngleXU=0 Radius=1.5
    g4: Circle CenterX=-7 CenterY=0 CenterZ=0 NormalX=0 NormalY=0 NormalZ=1 AngleXU=0 Radius=1.5
    g5: Circle [constr] CenterX=0 CenterY=0 CenterZ=0 NormalX=0 NormalY=0 NormalZ=1 AngleXU=0 Radius=7
    g6: Circle CenterX=0 CenterY=0 CenterZ=0 NormalX=0 NormalY=0 NormalZ=1 AngleXU=0 Radius=1.5
  constraints (18):
    c: Coincident(g0,g-1)
    c: Diameter(g0) = 20
    c: PointOnObject(g1,g-2)
    c: PointOnObject(g2,g-1)
    c: PointOnObject(g3,g-2)
    c: PointOnObject(g4,g-1)
    c: Equal(g4,g1)
    c: Equal(g1,g2)
    c: Equal(g2,g3)
    c: Diameter(g1) = 3
    c: Coincident(g5,g0)
    c: PointOnObject(g1,g5)
    c: PointOnObject(g2,g5)
    c: PointOnObject(g3,g5)
    c: PointOnObject(g4,g5)
    c: DistanceX(g4,g2) = 14
    c: Coincident(g6,g0)
    c: Equal(g2,g6)
FEATURE [PartDesign::Pad] Pad052
  AddSubType = 0
  AutoTaperInnerAngle = true
  CheckUpToFaceLimits = true
  ClaimChildren = false
  Direction = (0,0,1)
  Fit = 0
  FitJoin = 0
  FixShape = 1
  InnerFit = 0
  InnerFitJoin = 0
  InvalidShape = false
  Length = 2
  Length2 = 100
  NewSolid = false
  Profile = -> Sketch088
  Refine = true
  Reversed = true
  Suppress = false
  TaperInnerAngle = 0
  TaperInnerAngleRev = 0
  TreeRank = 0
  Type = 0
  ValidateShape = true
  _ProfileBasedVersion = 0
FEATURE [Sketcher::SketchObject] Sketch089
  ArcFitTolerance = 0
  ExternalBSplineMaxDegree = 0
  ExternalBSplineTolerance = 0
  FixShape = 1
  FullyConstrained = true
  InternalTolerance = 1e-06
  InvalidShape = false
  MakeInternals = false
  MapMode = 5
  TreeRank = 0
  ValidateShape = false
  sketch-geometry (2):
    g0: Circle CenterX=0 CenterY=0 CenterZ=0 NormalX=0 NormalY=0 NormalZ=1 AngleXU=0 Radius=4.7
    g1: Circle CenterX=0 CenterY=0 CenterZ=0 NormalX=0 NormalY=0 NormalZ=1 AngleXU=0 Radius=3
  constraints (4):
    c: Coincident(g0,g-1)
    c: Coincident(g1,g0)
    c: Diameter(g0) = 9.4
    c: Diameter(g1) = 6
FEATURE [PartDesign::Pad] Pad051
  AddSubType = 0
  AutoTaperInnerAngle = true
  BaseFeature = -> Pad052
  CheckUpToFaceLimits = true
  ClaimChildren = false
  Direction = (0,0,1)
  Fit = 0
  FitJoin = 0
  FixShape = 1
  InnerFit = 0
  InnerFitJoin = 0
  InvalidShape = false
  Length = 5.4
  Length2 = 100
  NewSolid = false
  Profile = -> Sketch089
  Refine = true
  Reversed = true
  Suppress = false
  TaperInnerAngle = 0
  TaperInnerAngleRev = 0
  TreeRank = 0
  Type = 0
  ValidateShape = true
  _ProfileBasedVersion = 0
FEATURE [PartDesign::Body] Body042  label="RoundServoHorn"
  AutoGroupSolids = false
  ClaimAllChildren = false
  ExportMode = 0
  FixShape = 1
  Group = -> [Sketch088,Pad052,Sketch089,Pad051]
  InvalidShape = false
  Origin = -> Origin063
  Placement = pos=(0,0,0) rot=(1,0,0;1.5708rad)
  SingleSolid = true
  Tip = -> Pad051
  TreeRank = 0
  ValidateShape = false
  _ExportChildren = -> [Pad052,Pad051]
  _GroupVersion = 1
COMPONENT P6 — recipe-attached ("ElasticServoHorn", modeled in this document).
Construction recipe (the document's own serialized feature program — sketch geometry with constraints, then the solid features built on it; lengths are millimeters unless a unit is written):

FEATURE [Sketcher::SketchObject] Sketch123
  ArcFitTolerance = 0
  ExternalBSplineMaxDegree = 0
  ExternalBSplineTolerance = 0
  FixShape = 1
  FullyConstrained = false
  InternalTolerance = 1e-06
  InvalidShape = false
  MakeInternals = false
  MapMode = 5
  Placement = pos=(0,0,0) rot=(1,0,0;1.5708rad)
  TreeRank = 0
  ValidateShape = false
  sketch-geometry (17):
    g0: ArcOfCircle CenterX=0 CenterY=0 CenterZ=0 NormalX=0 NormalY=0 NormalZ=1 AngleXU=0 Radius=8 StartAngle=5.67415 EndAngle=10.0338
    g1: ArcOfCircle CenterX=4.3e-15 CenterY=1 CenterZ=0 NormalX=0 NormalY=0 NormalZ=1 AngleXU=0 Radius=26 StartAngle=4.4405 EndAngle=4.98428
    g2: ArcOfCircle CenterX=6.42511 CenterY=-22.0462 CenterZ=0 NormalX=0 NormalY=0 NormalZ=1 AngleXU=0 Radius=2.07489 StartAngle=4.98428 EndAngle=6.60035
    g3: ArcOfCircle CenterX=-6.42511 CenterY=-22.0462 CenterZ=0 NormalX=0 NormalY=0 NormalZ=1 AngleXU=0 Radius=2.07489 StartAngle=2.82443 EndAngle=4.4405
    g4: LineSegment [constr] StartX=8.5 StartY=0 StartZ=0 EndX=8.5 EndY=-36.4357 EndZ=0
    g5: GeomPoint [constr] X=0 Y=-25 Z=0
    g6: GeomPoint [constr] X=0 Y=8 Z=0
    g7: Circle CenterX=-5.5 CenterY=-21 CenterZ=0 NormalX=0 NormalY=0 NormalZ=1 AngleXU=0 Radius=1.5
    g8: Circle CenterX=0 CenterY=-21 CenterZ=0 NormalX=0 NormalY=0 NormalZ=1 AngleXU=0 Radius=1.5
    g9: Circle CenterX=5.5 CenterY=-21 CenterZ=0 NormalX=0 NormalY=0 NormalZ=1 AngleXU=0 Radius=1.5
    g10: Circle CenterX=-4 CenterY=-17 CenterZ=0 NormalX=0 NormalY=0 NormalZ=1 AngleXU=0 Radius=1.5
    g11: Circle CenterX=4 CenterY=-17 CenterZ=0 NormalX=0 NormalY=0 NormalZ=1 AngleXU=0 Radius=1.5
    g12: LineSegment StartX=8.39651 StartY=-21.3991 StartZ=0 EndX=5.42127 EndY=-12.335 EndZ=0
    g13: LineSegment StartX=-8.39651 StartY=-21.3991 StartZ=0 EndX=-5.42127 EndY=-12.335 EndZ=0
    g14: ArcOfCircle CenterX=-13.7605 CenterY=-9.59771 CenterZ=0 NormalX=0 NormalY=0 NormalZ=1 AngleXU=0 Radius=8.777 StartAngle=5.96602 EndAngle=6.89222
    g15: ArcOfCircle CenterX=13.7605 CenterY=-9.59771 CenterZ=0 NormalX=0 NormalY=0 NormalZ=1 AngleXU=0 Radius=8.777 StartAngle=2.53256 EndAngle=3.45876
    g16: LineSegment [constr] StartX=-5 StartY=-9.06 StartZ=0 EndX=5 EndY=-9.06 EndZ=0
  constraints (43):
    c: Coincident(g0,g-1)
    c: Diameter(g0) = 16
    c: Symmetric(g1,g1,g-2)
    c: Tangent(g3,g1) = -1.5708
    c: Tangent(g2,g1) = -1.5708
    c: Symmetric(g3,g2,g-2)
    c: PointOnObject(g4,g-1)
    c: Vertical(g4)
    c: Tangent(g2,g4)
    c: DistanceX(g4) = 8.5
    c: PointOnObject(g5,g1)
    c: PointOnObject(g6,g0)
    c: PointOnObject(g6,g-2)
    c: PointOnObject(g5,g-2)
    c: DistanceY(g5,g6) = 33
    c: PointOnObject(g8,g-2)
    c: Horizontal(g7,g8)
    c: Symmetric(g10,g11,g-2)
    c: Symmetric(g7,g9,g-2)
    c: DistanceY(g11) = -17
    c: DistanceY(g9) = -21
    c: Diameter(g7) = 3
    c: Equal(g7,g10)
    c: Equal(g7,g8)
    c: Equal(g7,g9)
    c: Equal(g7,g11)
    c: DistanceX(g7,g9) = 11
    c: DistanceX(g10,g11) = 8
    c: Tangent(g13,g3) = 1.5708
    c: Tangent(g12,g2) = -1.5708
    c: Tangent(g15,g12) = 1.5708
    c: Tangent(g15,g0) = 1.5708
    c: PointOnObject(g16,g14)
    c: Horizontal(g16)
    c: PointOnObject(g16,g15)
    c: DistanceX(g16,g16) = 10
    c: Tangent(g14,g13) = -1.5708
    c: Tangent(g14,g0) = 1.5708
    c: Distance(g2,g1) = 3
    c: Diameter(g1) = 52
    c: Equal(g15,g14)
    c: DistanceY(g16,g0) = 9.06
    c: Radius(g15) = 8.777
FEATURE [PartDesign::Pad] Pad066
  AddSubType = 0
  AutoTaperInnerAngle = true
  CheckUpToFaceLimits = true
  ClaimChildren = false
  Direction = (0,-1,0)
  Fit = 0
  FitJoin = 0
  FixShape = 1
  InnerFit = 0
  InnerFitJoin = 0
  InvalidShape = false
  Length = 4
  Length2 = 100
  NewSolid = false
  Placement = pos=(0,0,0) rot=(1,0,0;1.5708rad)
  Profile = -> Sketch123
  Refine = true
  Reversed = true
  Suppress = false
  TaperInnerAngle = 0
  TaperInnerAngleRev = 0
  TreeRank = 0
  Type = 0
  ValidateShape = true
  _ProfileBasedVersion = 0
FEATURE [Sketcher::SketchObject] Sketch124
  ArcFitTolerance = 0
  ExternalBSplineMaxDegree = 0
  ExternalBSplineTolerance = 0
  FixShape = 1
  FullyConstrained = true
  InternalTolerance = 1e-06
  InvalidShape = false
  MakeInternals = false
  MapMode = 5
  Placement = pos=(0,0,0) rot=(1,0,0;1.5708rad)
  TreeRank = 0
  ValidateShape = false
  sketch-geometry (1):
    g0: Circle CenterX=0 CenterY=0 CenterZ=0 NormalX=0 NormalY=0 NormalZ=1 AngleXU=0 Radius=8
  constraints (2):
    c: Coincident(g0,g-1)
    c: Diameter(g0) = 16
FEATURE [PartDesign::Pad] Pad067
  AddSubType = 0
  AutoTaperInnerAngle = true
  BaseFeature = -> Pad066
  CheckUpToFaceLimits = true
  ClaimChildren = false
  Direction = (0,-1,0)
  Fit = 0
  FitJoin = 0
  FixShape = 1
  InnerFit = 0
  InnerFitJoin = 0
  InvalidShape = false
  Length = 10
  Length2 = 100
  NewSolid = false
  Placement = pos=(0,0,0) rot=(1,0,0;1.5708rad)
  Profile = -> Sketch124
  Refine = true
  Reversed = true
  Suppress = false
  TaperInnerAngle = 0
  TaperInnerAngleRev = 0
  TreeRank = 0
  Type = 0
  ValidateShape = true
  _ProfileBasedVersion = 0
FEATURE [Sketcher::SketchObject] Sketch125
  ArcFitTolerance = 0
  ExternalBSplineMaxDegree = 0
  ExternalBSplineTolerance = 0
  FixShape = 1
  FullyConstrained = true
  InternalTolerance = 1e-06
  InvalidShape = false
  MakeInternals = false
  MapMode = 5
  Placement = pos=(0,10,0) rot=(-1,0,0;1.5708rad)
  TreeRank = 0
  ValidateShape = false
  sketch-geometry (1):
    g0: Circle CenterX=0 CenterY=0 CenterZ=0 NormalX=0 NormalY=0 NormalZ=1 AngleXU=0 Radius=3
  constraints (2):
    c: Coincident(g0,g-1)
    c: Diameter(g0) = 6
FEATURE [PartDesign::Pocket] Pocket049
  AddSubType = 1
  AutoTaperInnerAngle = true
  BaseFeature = -> Pad067
  CheckUpToFaceLimits = true
  ClaimChildren = false
  Direction = (0,-1,0)
  Fit = 0
  FitJoin = 0
  FixShape = 1
  InnerFit = 0
  InnerFitJoin = 0
  InvalidShape = false
  Length = 3.2
  Length2 = 100
  NewSolid = false
  Placement = pos=(0,0,0) rot=(1,0,0;1.5708rad)
  Profile = -> Sketch125
  Refine = true
  Suppress = false
  TaperInnerAngle = 0
  TaperInnerAngleRev = 0
  TreeRank = 0
  Type = 0
  ValidateShape = true
  _ProfileBasedVersion = 0
  _Version = 0
FEATURE [Sketcher::SketchObject] Sketch126
  ArcFitTolerance = 0
  ExternalBSplineMaxDegree = 0
  ExternalBSplineTolerance = 0
  FixShape = 1
  FullyConstrained = true
  InternalTolerance = 1e-06
  InvalidShape = false
  MakeInternals = false
  MapMode = 5
  Placement = pos=(0,0,0) rot=(1,0,0;1.5708rad)
  TreeRank = 0
  ValidateShape = false
  sketch-geometry (1):
    g0: Circle CenterX=0 CenterY=0 CenterZ=0 NormalX=0 NormalY=0 NormalZ=1 AngleXU=0 Radius=1.5
  constraints (2):
    c: Coincident(g0,g-1)
    c: Diameter(g0) = 3
FEATURE [PartDesign::Pocket] Pocket050
  AddSubType = 1
  AutoTaperInnerAngle = true
  BaseFeature = -> Pocket049
  CheckUpToFaceLimits = true
  ClaimChildren = false
  Direction = (0,1,0)
  Fit = 0
  FitJoin = 0
  FixShape = 1
  InnerFit = 0
  InnerFitJoin = 0
  InvalidShape = false
  Length = 5
  Length2 = 100
  NewSolid = false
  Placement = pos=(0,0,0) rot=(1,0,0;1.5708rad)
  Profile = -> Sketch126
  Refine = true
  Suppress = false
  TaperInnerAngle = 0
  TaperInnerAngleRev = 0
  TreeRank = 0
  Type = 1
  ValidateShape = true
  _ProfileBasedVersion = 0
  _Version = 0
FEATURE [Sketcher::SketchObject] Sketch127
  ArcFitTolerance = 0
  ExternalBSplineMaxDegree = 0
  ExternalBSplineTolerance = 0
  FixShape = 1
  FullyConstrained = true
  InternalTolerance = 1e-06
  InvalidShape = false
  MakeInternals = false
  MapMode = 5
  Placement = pos=(0,0,0) rot=(1,0,0;1.5708rad)
  TreeRank = 0
  ValidateShape = false
  sketch-geometry (1):
    g0: Circle CenterX=0 CenterY=0 CenterZ=0 NormalX=0 NormalY=0 NormalZ=1 AngleXU=0 Radius=3.75
  constraints (2):
    c: Coincident(g0,g-1)
    c: Diameter(g0) = 7.5
FEATURE [PartDesign::Pocket] Pocket051
  AddSubType = 1
  AutoTaperInnerAngle = true
  BaseFeature = -> Pocket050
  CheckUpToFaceLimits = true
  ClaimChildren = false
  Direction = (0,1,0)
  Fit = 0
  FitJoin = 0
  FixShape = 1
  InnerFit = 0
  InnerFitJoin = 0
  InvalidShape = false
  Length = 4
  Length2 = 100
  NewSolid = false
  Placement = pos=(0,0,0) rot=(1,0,0;1.5708rad)
  Profile = -> Sketch127
  Refine = true
  Suppress = false
  TaperInnerAngle = 0
  TaperInnerAngleRev = 0
  TreeRank = 0
  Type = 0
  ValidateShape = true
  _ProfileBasedVersion = 0
  _Version = 0
FEATURE [PartDesign::Chamfer] Chamfer040
  AddSubType = 0
  Angle = 45
  Base = -> Pocket051 [Edge24,Edge14]
  BaseFeature = -> Pocket051
  ChamferType = 0
  FixShape = 1
  FlipDirection = false
  InvalidShape = false
  NewSolid = false
  Placement = pos=(0,0,0) rot=(1,0,0;1.5708rad)
  Refine = true
  Size = 0.2
  Size2 = 1
  SupportTransform = false
  Suppress = false
  TreeRank = 0
  UseAllEdges = false
  ValidateShape = true
FEATURE [PartDesign::Chamfer] Chamfer041
  AddSubType = 0
  Angle = 45
  Base = -> Chamfer040 [Edge25]
  BaseFeature = -> Chamfer040
  ChamferType = 0
  FixShape = 1
  FlipDirection = false
  InvalidShape = false
  NewSolid = false
  Placement = pos=(0,0,0) rot=(1,0,0;1.5708rad)
  Refine = true
  Size = 0.2
  Size2 = 1
  SupportTransform = false
  Suppress = false
  TreeRank = 0
  UseAllEdges = false
  ValidateShape = true
FEATURE [PartDesign::Body] Body057  label="ElasticServoHorn"
  AutoGroupSolids = false
  ClaimAllChildren = false
  ExportMode = 0
  FixShape = 1
  Group = -> [Sketch123,Pad066,Sketch124,Pad067,Sketch125,Pocket049,Sketch126,Pocket050,Sketch127,Pocket051,Chamfer040,Chamfer041]
  InvalidShape = false
  Origin = -> Origin085
  Placement = pos=(-1.09497e-05,-4.80001,-1.51983e-05) rot=(0,1,0;1.5708rad)
  SingleSolid = true
  Tip = -> Chamfer041
  TreeRank = 0
  ValidateShape = false
  _ExportChildren = -> [Pad066,Pad067,Pocket049,Pocket050,Pocket051,Chamfer040,Chamfer041]
  _GroupVersion = 1
COMPONENT P7 — recipe-attached ("MB_150", modeled in this document).
Construction recipe (the document's own serialized feature program — sketch geometry with constraints, then the solid features built on it; lengths are millimeters unless a unit is written):

FEATURE [PartDesign::CoordinateSystem] Local_CS003
  AttacherType = Attacher::AttachEngine3D
  FixShape = 1
  InvalidShape = false
  MapMode = 11
  Placement = pos=(0,150,-3.3e-14) rot=(0.57735,0.57735,-0.57735;2.0944rad)
  TreeRank = 0
  ValidateShape = false
FEATURE [Sketcher::SketchObject] Sketch200
  ArcFitTolerance = 0
  ExternalBSplineMaxDegree = 0
  ExternalBSplineTolerance = 0
  FixShape = 1
  FullyConstrained = true
  InternalTolerance = 1e-06
  InvalidShape = false
  MakeInternals = false
  MapMode = 5
  Placement = pos=(0,0,0) rot=(1,0,0;1.5708rad)
  TreeRank = 0
  ValidateShape = false
  sketch-geometry (14):
    g0: ArcOfCircle CenterX=0 CenterY=0 CenterZ=0 NormalX=0 NormalY=0 NormalZ=1 AngleXU=0 Radius=1.25 StartAngle=0 EndAngle=1.5708
    g1: LineSegment StartX=1e-16 StartY=1.25 StartZ=0 EndX=0 EndY=2 EndZ=0
    g2: LineSegment StartX=0 StartY=2 StartZ=0 EndX=1 EndY=2 EndZ=0
    g3: LineSegment [constr] StartX=0 StartY=0 StartZ=0 EndX=5 EndY=5 EndZ=0
    g4: LineSegment StartX=1 StartY=2 StartZ=0 EndX=3.3 EndY=4 EndZ=0
    g5: LineSegment StartX=3.3 StartY=4 StartZ=0 EndX=1.5 EndY=4 EndZ=0
    g6: LineSegment StartX=1.5 StartY=4 StartZ=0 EndX=1.5 EndY=5 EndZ=0
    g7: LineSegment StartX=1.5 StartY=5 StartZ=0 EndX=5 EndY=5 EndZ=0
    g8: LineSegment StartX=5 StartY=5 StartZ=0 EndX=5 EndY=1.5 EndZ=0
    g9: LineSegment StartX=5 StartY=1.5 StartZ=0 EndX=4 EndY=1.5 EndZ=0
    g10: LineSegment StartX=4 StartY=1.5 StartZ=0 EndX=4 EndY=3.3 EndZ=0
    g11: LineSegment StartX=4 StartY=3.3 StartZ=0 EndX=2 EndY=1 EndZ=0
    g12: LineSegment StartX=2 StartY=1 StartZ=0 EndX=2 EndY=0 EndZ=0
    g13: LineSegment StartX=2 StartY=0 StartZ=0 EndX=1.25 EndY=0 EndZ=0
  constraints (41):
    c: Coincident(g0,g-1)
    c: PointOnObject(g0,g-1)
    c: PointOnObject(g0,g-2)
    c: Coincident(g1,g0)
    c: PointOnObject(g1,g-2)
    c: Coincident(g2,g1)
    c: Horizontal(g2)
    c: Coincident(g3,g0)
    c: Angle(g-1,g3) = 0.785398
    c: DistanceX(g3) = 5
    c: Diameter(g0) = 2.5
    c: DistanceX(g2) = 1
    c: Coincident(g4,g2)
    c: Coincident(g5,g4)
    c: Horizontal(g5)
    c: Coincident(g6,g5)
    c: Vertical(g6)
    c: Coincident(g7,g6)
    c: Coincident(g7,g3)
    c: Coincident(g8,g7)
    c: Vertical(g8)
    c: Coincident(g9,g8)
    c: Coincident(g10,g9)
    c: Vertical(g10)
    c: Coincident(g11,g10)
    c: Coincident(g12,g11)
    c: PointOnObject(g12,g-1)
    c: Vertical(g12)
    c: Coincident(g13,g12)
    c: Coincident(g13,g0)
    c: Equal(g12,g2)
    c: Equal(g13,g1)
    c: Horizontal(g7)
    c: Horizontal(g9)
    c: Equal(g6,g9)
    c: Equal(g11,g4)
    c: Equal(g5,g10)
    c: DistanceY(g2,g6) = 3
    c: DistanceX(g6) = 1.5
    c: DistanceY(g6,g6) = 1
    c: DistanceX(g5,g5) = 1.8
FEATURE [PartDesign::Pad] Pad081
  AddSubType = 0
  AlongSketchNormal = false
  AutoTaperInnerAngle = true
  CheckUpToFaceLimits = true
  ClaimChildren = false
  Direction = (0,-1,0)
  Fit = 0
  FitJoin = 0
  FixShape = 1
  InnerFit = 0
  InnerFitJoin = 0
  InvalidShape = false
  Length = 150
  Length2 = 100
  NewSolid = false
  Placement = pos=(0,0,0) rot=(1,0,0;1.5708rad)
  Profile = -> Sketch200
  Refine = true
  Reversed = true
  Suppress = false
  TaperInnerAngle = 0
  TaperInnerAngleRev = 0
  TreeRank = 0
  Type = 0
  ValidateShape = true
  _ProfileBasedVersion = 0
FEATURE [PartDesign::PolarPattern] PolarPattern013
  AddSubType = 0
  Angle = 360
  Axis = -> Y_Axis115
  BaseFeature = -> Pad081
  CopyShape = true
  FixShape = 1
  InvalidShape = false
  NewSolid = false
  Occurrences = 4
  OriginalSubs = -> [Pad081]
  Originals = -> [Pad081]
  ParallelTransform = true
  Placement = pos=(0,0,0) rot=(1,0,0;1.5708rad)
  Refine = true
  SubTransform = true
  Suppress = false
  TreeRank = 0
  ValidateShape = true
  _Version = 0
FEATURE [PartDesign::Body] Body095  label="MB_150"
  AutoGroupSolids = false
  ClaimAllChildren = false
  ExportMode = 0
  FixShape = 1
  Group = -> [Sketch200,Pad081,PolarPattern013,Local_CS003]
  InvalidShape = false
  Origin = -> Origin185
  SingleSolid = true
  Tip = -> PolarPattern013
  TreeRank = 0
  ValidateShape = false
  _ExportChildren = -> [Pad081,PolarPattern013,Local_CS003]
  _GroupVersion = 1
COMPONENT P8 — recipe-attached ("MB_200", modeled in this document).
Construction recipe (the document's own serialized feature program — sketch geometry with constraints, then the solid features built on it; lengths are millimeters unless a unit is written):

FEATURE [PartDesign::CoordinateSystem] Local_CS004
  AttacherType = Attacher::AttachEngine3D
  FixShape = 1
  InvalidShape = false
  MapMode = 11
  Placement = pos=(0,200,-4.4e-14) rot=(0.57735,0.57735,-0.57735;2.0944rad)
  TreeRank = 0
  ValidateShape = false
FEATURE [Sketcher::SketchObject] Sketch201
  ArcFitTolerance = 0
  ExternalBSplineMaxDegree = 0
  ExternalBSplineTolerance = 0
  FixShape = 1
  FullyConstrained = true
  InternalTolerance = 1e-06
  InvalidShape = false
  MakeInternals = false
  MapMode = 5
  Placement = pos=(0,0,0) rot=(1,0,0;1.5708rad)
  TreeRank = 0
  ValidateShape = false
  sketch-geometry (14):
    g0: ArcOfCircle CenterX=0 CenterY=0 CenterZ=0 NormalX=0 NormalY=0 NormalZ=1 AngleXU=0 Radius=1.25 StartAngle=0 EndAngle=1.5708
    g1: LineSegment StartX=1e-16 StartY=1.25 StartZ=0 EndX=0 EndY=2 EndZ=0
    g2: LineSegment StartX=0 StartY=2 StartZ=0 EndX=1 EndY=2 EndZ=0
    g3: LineSegment [constr] StartX=0 StartY=0 StartZ=0 EndX=5 EndY=5 EndZ=0
    g4: LineSegment StartX=1 StartY=2 StartZ=0 EndX=3.3 EndY=4 EndZ=0
    g5: LineSegment StartX=3.3 StartY=4 StartZ=0 EndX=1.5 EndY=4 EndZ=0
    g6: LineSegment StartX=1.5 StartY=4 StartZ=0 EndX=1.5 EndY=5 EndZ=0
    g7: LineSegment StartX=1.5 StartY=5 StartZ=0 EndX=5 EndY=5 EndZ=0
    g8: LineSegment StartX=5 StartY=5 StartZ=0 EndX=5 EndY=1.5 EndZ=0
    g9: LineSegment StartX=5 StartY=1.5 StartZ=0 EndX=4 EndY=1.5 EndZ=0
    g10: LineSegment StartX=4 StartY=1.5 StartZ=0 EndX=4 EndY=3.3 EndZ=0
    g11: LineSegment StartX=4 StartY=3.3 StartZ=0 EndX=2 EndY=1 EndZ=0
    g12: LineSegment StartX=2 StartY=1 StartZ=0 EndX=2 EndY=0 EndZ=0
    g13: LineSegment StartX=2 StartY=0 StartZ=0 EndX=1.25 EndY=0 EndZ=0
  constraints (41):
    c: Coincident(g0,g-1)
    c: PointOnObject(g0,g-1)
    c: PointOnObject(g0,g-2)
    c: Coincident(g1,g0)
    c: PointOnObject(g1,g-2)
    c: Coincident(g2,g1)
    c: Horizontal(g2)
    c: Coincident(g3,g0)
    c: Angle(g-1,g3) = 0.785398
    c: DistanceX(g3) = 5
    c: Diameter(g0) = 2.5
    c: DistanceX(g2) = 1
    c: Coincident(g4,g2)
    c: Coincident(g5,g4)
    c: Horizontal(g5)
    c: Coincident(g6,g5)
    c: Vertical(g6)
    c: Coincident(g7,g6)
    c: Coincident(g7,g3)
    c: Coincident(g8,g7)
    c: Vertical(g8)
    c: Coincident(g9,g8)
    c: Coincident(g10,g9)
    c: Vertical(g10)
    c: Coincident(g11,g10)
    c: Coincident(g12,g11)
    c: PointOnObject(g12,g-1)
    c: Vertical(g12)
    c: Coincident(g13,g12)
    c: Coincident(g13,g0)
    c: Equal(g12,g2)
    c: Equal(g13,g1)
    c: Horizontal(g7)
    c: Horizontal(g9)
    c: Equal(g6,g9)
    c: Equal(g11,g4)
    c: Equal(g5,g10)
    c: DistanceY(g2,g6) = 3
    c: DistanceX(g6) = 1.5
    c: DistanceY(g6,g6) = 1
    c: DistanceX(g5,g5) = 1.8
FEATURE [PartDesign::Pad] Pad082
  AddSubType = 0
  AlongSketchNormal = false
  AutoTaperInnerAngle = true
  CheckUpToFaceLimits = true
  ClaimChildren = false
  Direction = (0,-1,0)
  Fit = 0
  FitJoin = 0
  FixShape = 1
  InnerFit = 0
  InnerFitJoin = 0
  InvalidShape = false
  Length = 200
  Length2 = 100
  NewSolid = false
  Placement = pos=(0,0,0) rot=(1,0,0;1.5708rad)
  Profile = -> Sketch201
  Refine = true
  Reversed = true
  Suppress = false
  TaperInnerAngle = 0
  TaperInnerAngleRev = 0
  TreeRank = 0
  Type = 0
  ValidateShape = true
  _ProfileBasedVersion = 0
FEATURE [PartDesign::PolarPattern] PolarPattern014
  AddSubType = 0
  Angle = 360
  Axis = -> Y_Axis116
  BaseFeature = -> Pad082
  CopyShape = true
  FixShape = 1
  InvalidShape = false
  NewSolid = false
  Occurrences = 4
  OriginalSubs = -> [Pad082]
  Originals = -> [Pad082]
  ParallelTransform = true
  Placement = pos=(0,0,0) rot=(1,0,0;1.5708rad)
  Refine = true
  SubTransform = true
  Suppress = false
  TreeRank = 0
  ValidateShape = true
  _Version = 0
FEATURE [PartDesign::Body] Body096  label="MB_200"
  AutoGroupSolids = false
  ClaimAllChildren = false
  ExportMode = 0
  FixShape = 1
  Group = -> [Sketch201,Pad082,PolarPattern014,Local_CS004]
  InvalidShape = false
  Origin = -> Origin186
  SingleSolid = true
  Tip = -> PolarPattern014
  TreeRank = 0
  ValidateShape = false
  _ExportChildren = -> [Pad082,PolarPattern014,Local_CS004]
  _GroupVersion = 1
COMPONENT P9 — recipe-attached ("MB_40", modeled in this document).
Construction recipe (the document's own serialized feature program — sketch geometry with constraints, then the solid features built on it; lengths are millimeters unless a unit is written):

FEATURE [PartDesign::CoordinateSystem] Local_CS005
  AttacherType = Attacher::AttachEngine3D
  FixShape = 1
  InvalidShape = false
  MapMode = 11
  Placement = pos=(0,40,-1.8e-14) rot=(1,0,0;1.5708rad)
  TreeRank = 0
  ValidateShape = false
FEATURE [Sketcher::SketchObject] Sketch211
  ArcFitTolerance = 0
  ExternalBSplineMaxDegree = 0
  ExternalBSplineTolerance = 0
  FixShape = 1
  FullyConstrained = true
  InternalTolerance = 1e-06
  InvalidShape = false
  MakeInternals = false
  MapMode = 5
  Placement = pos=(0,0,0) rot=(1,0,0;1.5708rad)
  TreeRank = 0
  ValidateShape = false
  sketch-geometry (14):
    g0: ArcOfCircle CenterX=0 CenterY=0 CenterZ=0 NormalX=0 NormalY=0 NormalZ=1 AngleXU=0 Radius=1.25 StartAngle=0 EndAngle=1.5708
    g1: LineSegment StartX=1e-16 StartY=1.25 StartZ=0 EndX=0 EndY=2 EndZ=0
    g2: LineSegment StartX=0 StartY=2 StartZ=0 EndX=1 EndY=2 EndZ=0
    g3: LineSegment [constr] StartX=0 StartY=0 StartZ=0 EndX=5 EndY=5 EndZ=0
    g4: LineSegment StartX=1 StartY=2 StartZ=0 EndX=3.3 EndY=4 EndZ=0
    g5: LineSegment StartX=3.3 StartY=4 StartZ=0 EndX=1.5 EndY=4 EndZ=0
    g6: LineSegment StartX=1.5 StartY=4 StartZ=0 EndX=1.5 EndY=5 EndZ=0
    g7: LineSegment StartX=1.5 StartY=5 StartZ=0 EndX=5 EndY=5 EndZ=0
    g8: LineSegment StartX=5 StartY=5 StartZ=0 EndX=5 EndY=1.5 EndZ=0
    g9: LineSegment StartX=5 StartY=1.5 StartZ=0 EndX=4 EndY=1.5 EndZ=0
    g10: LineSegment StartX=4 StartY=1.5 StartZ=0 EndX=4 EndY=3.3 EndZ=0
    g11: LineSegment StartX=4 StartY=3.3 StartZ=0 EndX=2 EndY=1 EndZ=0
    g12: LineSegment StartX=2 StartY=1 StartZ=0 EndX=2 EndY=0 EndZ=0
    g13: LineSegment StartX=2 StartY=0 StartZ=0 EndX=1.25 EndY=0 EndZ=0
  constraints (41):
    c: Coincident(g0,g-1)
    c: PointOnObject(g0,g-1)
    c: PointOnObject(g0,g-2)
    c: Coincident(g1,g0)
    c: PointOnObject(g1,g-2)
    c: Coincident(g2,g1)
    c: Horizontal(g2)
    c: Coincident(g3,g0)
    c: Angle(g-1,g3) = 0.785398
    c: DistanceX(g3) = 5
    c: Diameter(g0) = 2.5
    c: DistanceX(g2) = 1
    c: Coincident(g4,g2)
    c: Coincident(g5,g4)
    c: Horizontal(g5)
    c: Coincident(g6,g5)
    c: Vertical(g6)
    c: Coincident(g7,g6)
    c: Coincident(g7,g3)
    c: Coincident(g8,g7)
    c: Vertical(g8)
    c: Coincident(g9,g8)
    c: Coincident(g10,g9)
    c: Vertical(g10)
    c: Coincident(g11,g10)
    c: Coincident(g12,g11)
    c: PointOnObject(g12,g-1)
    c: Vertical(g12)
    c: Coincident(g13,g12)
    c: Coincident(g13,g0)
    c: Equal(g12,g2)
    c: Equal(g13,g1)
    c: Horizontal(g7)
    c: Horizontal(g9)
    c: Equal(g6,g9)
    c: Equal(g11,g4)
    c: Equal(g5,g10)
    c: DistanceY(g2,g6) = 3
    c: DistanceX(g6) = 1.5
    c: DistanceY(g6,g6) = 1
    c: DistanceX(g5,g5) = 1.8
FEATURE [PartDesign::Pad] Pad086
  AddSubType = 0
  AutoTaperInnerAngle = true
  CheckUpToFaceLimits = true
  ClaimChildren = false
  Direction = (0,-1,0)
  Fit = 0
  FitJoin = 0
  FixShape = 1
  InnerFit = 0
  InnerFitJoin = 0
  InvalidShape = false
  Length = 40
  Length2 = 100
  NewSolid = false
  Placement = pos=(0,0,0) rot=(1,0,0;1.5708rad)
  Profile = -> Sketch211
  ReferenceAxis = -> Sketch211 [N_Axis]
  Refine = true
  Reversed = true
  Suppress = false
  TaperInnerAngle = 0
  TaperInnerAngleRev = 0
  TreeRank = 0
  Type = 0
  ValidateShape = true
  _ProfileBasedVersion = 0
FEATURE [PartDesign::PolarPattern] PolarPattern021
  AddSubType = 0
  Angle = 360
  AttacherType = Attacher::AttachEngine3D
  Axis = -> Y_Axis125
  BaseFeature = -> Pad086
  CopyShape = true
  FixShape = 1
  InvalidShape = false
  NewSolid = false
  Occurrences = 4
  OriginalSubs = -> [Pad086]
  Originals = -> [Pad086]
  ParallelTransform = true
  Placement = pos=(0,0,0) rot=(1,0,0;1.5708rad)
  Refine = true
  SubTransform = true
  Suppress = false
  TreeRank = 0
  ValidateShape = true
  _Version = 0
FEATURE [PartDesign::Body] Body103  label="MB_40"
  AutoGroupSolids = false
  ClaimAllChildren = false
  ExportMode = 0
  FixShape = 1
  Group = -> [Sketch211,Pad086,PolarPattern021,Local_CS005]
  InvalidShape = false
  Origin = -> Origin202
  SingleSolid = true
  Tip = -> PolarPattern021
  TreeRank = 0
  ValidateShape = false
  _ExportChildren = -> [Pad086,PolarPattern021,Local_CS005]
  _GroupVersion = 1
COMPONENT P10 — recipe-attached ("Link_100_deg", modeled in this document).
Construction recipe (the document's own serialized feature program — sketch geometry with constraints, then the solid features built on it; lengths are millimeters unless a unit is written):

FEATURE [Sketcher::SketchObject] Sketch221
  ArcFitTolerance = 0
  ExternalBSplineMaxDegree = 0
  ExternalBSplineTolerance = 0
  FixShape = 1
  FullyConstrained = true
  InternalTolerance = 1e-06
  InvalidShape = false
  MakeInternals = false
  MapMode = 5
  Placement = pos=(0,0,0) rot=(0.57735,0.57735,0.57735;2.0944rad)
  TreeRank = 0
  ValidateShape = false
  sketch-geometry (5):
    g0: LineSegment StartX=-5 StartY=-5 StartZ=0 EndX=5 EndY=-5 EndZ=0
    g1: LineSegment StartX=5 StartY=-5 StartZ=0 EndX=5 EndY=5 EndZ=0
    g2: LineSegment StartX=5 StartY=5 StartZ=0 EndX=-5 EndY=5 EndZ=0
    g3: LineSegment StartX=-5 StartY=5 StartZ=0 EndX=-5 EndY=-5 EndZ=0
    g4: GeomPoint [constr] X=0 Y=0 Z=0
  constraints (12):
    c: Coincident(g0,g1)
    c: Coincident(g1,g2)
    c: Coincident(g2,g3)
    c: Coincident(g3,g0)
    c: Horizontal(g0)
    c: Horizontal(g2)
    c: Vertical(g1)
    c: Vertical(g3)
    c: Symmetric(g2,g0,g4)
    c: Coincident(g4,g-1)
    c: Equal(g1,g2)
    c: DistanceX(g2,g2) = 10
FEATURE [PartDesign::Pad] Pad090
  AddSubType = 0
  AutoTaperInnerAngle = true
  CheckUpToFaceLimits = true
  ClaimChildren = false
  Direction = (1,1e-16,-1e-16)
  Fit = 0
  FitJoin = 0
  FixShape = 1
  InnerFit = 0
  InnerFitJoin = 0
  InvalidShape = false
  Length = 10
  Length2 = 10
  Midplane = true
  NewSolid = false
  Placement = pos=(0,0,0) rot=(0.57735,0.57735,0.57735;2.0944rad)
  Profile = -> Sketch221
  ReferenceAxis = -> Sketch221 [N_Axis]
  Refine = true
  Suppress = false
  TaperInnerAngle = 0
  TaperInnerAngleRev = 0
  TreeRank = 0
  Type = 0
  ValidateShape = true
  _ProfileBasedVersion = 0
FEATURE [Sketcher::SketchObject] Sketch222
  ArcFitTolerance = 0
  ExternalBSplineMaxDegree = 0
  ExternalBSplineTolerance = 0
  FixShape = 1
  FullyConstrained = true
  InternalTolerance = 1e-06
  InvalidShape = false
  MakeInternals = false
  MapMode = 5
  Placement = pos=(0,0,0) rot=(0.57735,0.57735,0.57735;2.0944rad)
  TreeRank = 0
  ValidateShape = false
  sketch-geometry (1):
    g0: Circle CenterX=0 CenterY=0 CenterZ=0 NormalX=0 NormalY=0 NormalZ=1 AngleXU=0 Radius=1.5
  constraints (2):
    c: Coincident(g0,g-1)
    c: Diameter(g0) = 3
FEATURE [PartDesign::Pocket] Pocket067
  AddSubType = 1
  AutoTaperInnerAngle = true
  BaseFeature = -> Pad090
  CheckUpToFaceLimits = true
  ClaimChildren = false
  Direction = (-1,-1e-16,1e-16)
  Fit = 0
  FitJoin = 0
  FixShape = 1
  InnerFit = 0
  InnerFitJoin = 0
  InvalidShape = false
  Length = 5
  Length2 = 5
  Midplane = true
  NewSolid = false
  Placement = pos=(0,0,0) rot=(0.57735,0.57735,0.57735;2.0944rad)
  Profile = -> Sketch222
  ReferenceAxis = -> Sketch222 [N_Axis]
  Refine = true
  Suppress = false
  TaperInnerAngle = 0
  TaperInnerAngleRev = 0
  TreeRank = 0
  Type = 1
  ValidateShape = true
  _ProfileBasedVersion = 0
  _Version = 0
FEATURE [Sketcher::SketchObject] Sketch223
  ArcFitTolerance = 0
  ExternalBSplineMaxDegree = 0
  ExternalBSplineTolerance = 0
  FixShape = 1
  FullyConstrained = true
  InternalTolerance = 1e-06
  InvalidShape = false
  MakeInternals = false
  MapMode = 5
  TreeRank = 0
  ValidateShape = false
  sketch-geometry (1):
    g0: Circle CenterX=0 CenterY=0 CenterZ=0 NormalX=0 NormalY=0 NormalZ=1 AngleXU=0 Radius=1.5
  constraints (2):
    c: Coincident(g0,g-1)
    c: Diameter(g0) = 3
FEATURE [PartDesign::Pocket] Pocket068
  AddSubType = 1
  AutoTaperInnerAngle = true
  BaseFeature = -> Pocket067
  CheckUpToFaceLimits = true
  ClaimChildren = false
  Direction = (0,0,-1)
  Fit = 0
  FitJoin = 0
  FixShape = 1
  InnerFit = 0
  InnerFitJoin = 0
  InvalidShape = false
  Length = 5
  Length2 = 5
  Midplane = true
  NewSolid = false
  Placement = pos=(0,0,0) rot=(0.57735,0.57735,0.57735;2.0944rad)
  Profile = -> Sketch223
  ReferenceAxis = -> Sketch223 [N_Axis]
  Refine = true
  Suppress = false
  TaperInnerAngle = 0
  TaperInnerAngleRev = 0
  TreeRank = 0
  Type = 1
  ValidateShape = true
  _ProfileBasedVersion = 0
  _Version = 0
FEATURE [Sketcher::SketchObject] Sketch224
  ArcFitTolerance = 0
  ExternalBSplineMaxDegree = 0
  ExternalBSplineTolerance = 0
  ExternalGeometry = -> [Pocket068]
  FixShape = 1
  FullyConstrained = true
  InternalTolerance = 1e-06
  InvalidShape = false
  MakeInternals = false
  MapMode = 5
  Placement = pos=(0,0,0) rot=(0.57735,0.57735,0.57735;2.0944rad)
  TreeRank = 0
  ValidateShape = false
  sketch-geometry (6):
    g0: LineSegment StartX=5 StartY=-5 StartZ=0 EndX=5 EndY=5 EndZ=0
    g1: LineSegment StartX=5 StartY=5 StartZ=0 EndX=20.4122 EndY=5 EndZ=0
    g2: LineSegment StartX=20.4122 StartY=5 StartZ=0 EndX=22.3228 EndY=-5.83584 EndZ=0
    g3: LineSegment StartX=22.3228 StartY=-5.83584 StartZ=0 EndX=12.4748 EndY=-7.57232 EndZ=0
    g4: LineSegment StartX=12.4748 StartY=-7.57232 StartZ=0 EndX=12.0212 EndY=-5 EndZ=0
    g5: LineSegment StartX=12.0212 StartY=-5 StartZ=0 EndX=5 EndY=-5 EndZ=0
  constraints (16):
    c: Coincident(g-3,g0)
    c: Coincident(g0,g-3)
    c: Coincident(g0,g1)
    c: Horizontal(g1)
    c: Coincident(g1,g2)
    c: Coincident(g2,g3)
    c: Coincident(g3,g4)
    c: Coincident(g4,g5)
    c: Coincident(g5,g0)
    c: Horizontal(g5)
    c: Distance(g3,g3) = 10
    c: Perpendicular(g3,g2)
    c: Perpendicular(g3,g4)
    c: Angle(g5,g4) = 1.74533
    c: Distance(g3,g0) = 7.905
    c: Distance(g0,g2) = 17.343
FEATURE [PartDesign::Pad] Pad091
  AddSubType = 0
  AutoTaperInnerAngle = true
  BaseFeature = -> Pocket068
  CheckUpToFaceLimits = true
  ClaimChildren = false
  Direction = (1,1e-16,-1e-16)
  Fit = 0
  FitJoin = 0
  FixShape = 1
  InnerFit = 0
  InnerFitJoin = 0
  InvalidShape = false
  Length = 10
  Length2 = 10
  Midplane = true
  NewSolid = false
  Placement = pos=(0,0,0) rot=(0.57735,0.57735,0.57735;2.0944rad)
  Profile = -> Sketch224
  ReferenceAxis = -> Sketch224 [N_Axis]
  Refine = true
  Suppress = false
  TaperInnerAngle = 0
  TaperInnerAngleRev = 0
  TreeRank = 0
  Type = 0
  ValidateShape = true
  _ProfileBasedVersion = 0
FEATURE [Sketcher::SketchObject] Sketch225
  ArcFitTolerance = 0
  ExternalBSplineMaxDegree = 0
  ExternalBSplineTolerance = 0
  ExternalGeometry = -> [Pad091]
  FixShape = 1
  FullyConstrained = true
  InternalTolerance = 1e-06
  InvalidShape = false
  MakeInternals = false
  MapMode = 5
  Placement = pos=(0,0,0) rot=(0.57735,0.57735,0.57735;2.0944rad)
  TreeRank = 0
  ValidateShape = false
  sketch-geometry (7):
    g0: LineSegment [constr] StartX=15.3351 StartY=5 StartZ=0 EndX=17.3988 EndY=-6.70408 EndZ=0
    g1: LineSegment StartX=15.9216 StartY=-6.96456 StartZ=0 EndX=17.3988 EndY=-6.70408 EndZ=0
    g2: LineSegment StartX=17.3988 StartY=-6.70408 StartZ=0 EndX=15.2371 EndY=5.55567 EndZ=0
    g3: LineSegment StartX=15.2371 StartY=5.55567 StartZ=0 EndX=12.0857 EndY=5 EndZ=0
    g4: LineSegment StartX=12.0857 StartY=5 StartZ=0 EndX=13.6049 EndY=-3.61597 EndZ=0
    g5: LineSegment StartX=13.6049 StartY=-3.61597 StartZ=0 EndX=15.5743 EndY=-4.99494 EndZ=0
    g6: LineSegment StartX=15.5743 StartY=-4.99494 StartZ=0 EndX=15.9216 EndY=-6.96456 EndZ=0
  constraints (20):
    c: PointOnObject(g0,g-4)
    c: Symmetric(g-3,g-3,g0)
    c: Perpendicular(g-3,g0)
    c: PointOnObject(g1,g-3)
    c: Coincident(g1,g0)
    c: Coincident(g1,g2)
    c: Coincident(g2,g3)
    c: Coincident(g3,g4)
    c: Coincident(g4,g5)
    c: Coincident(g5,g6)
    c: Coincident(g6,g1)
    c: Perpendicular(g6,g1)
    c: Distance(g1,g1) = 1.5
    c: Distance(g6,g6) = 2
    c: Angle(g6,g5) = 0.785398
    c: Perpendicular(g4,g3)
    c: Distance(g3,g3) = 3.2
    c: PointOnObject(g0,g2)
    c: Perpendicular(g2,g3)
    c: PointOnObject(g3,g-4)
FEATURE [PartDesign::Groove] Groove002
  AddSubType = 1
  Angle = 360
  Axis = (-1.5e-15,2.06375,-11.7041)
  Base = (-1.1e-15,15.3351,5)
  BaseFeature = -> Pad091
  ClaimChildren = false
  Fit = 0
  FitJoin = 0
  FixShape = 1
  InnerFit = 0
  InnerFitJoin = 0
  InvalidShape = false
  NewSolid = false
  Placement = pos=(0,0,0) rot=(0.57735,0.57735,0.57735;2.0944rad)
  Profile = -> Sketch225
  ReferenceAxis = -> Sketch225 [Axis]
  Refine = true
  Suppress = false
  TreeRank = 0
  ValidateShape = true
  _ProfileBasedVersion = 0
FEATURE [Sketcher::SketchObject] Sketch226
  ArcFitTolerance = 0
  AttachmentSupport = -> [Groove002]
  ExternalBSplineMaxDegree = 0
  ExternalBSplineTolerance = 0
  FixShape = 1
  FullyConstrained = true
  InternalTolerance = 1e-06
  InvalidShape = false
  MakeInternals = false
  MapMode = 5
  Placement = pos=(3.5e-15,-1.9e-15,5) rot=(0,0,-1;1.5708rad)
  Support = -> [Groove002]
  TreeRank = 0
  ValidateShape = false
  sketch-geometry (1):
    g0: Circle CenterX=0 CenterY=0 CenterZ=0 NormalX=0 NormalY=0 NormalZ=1 AngleXU=0 Radius=3.2
  constraints (2):
    c: Coincident(g0,g-1)
    c: Diameter(g0) = 6.4
FEATURE [PartDesign::Pocket] Pocket069
  AddSubType = 1
  AutoTaperInnerAngle = true
  BaseFeature = -> Groove002
  CheckUpToFaceLimits = true
  ClaimChildren = false
  Direction = (-7e-16,4e-16,-1)
  Fit = 0
  FitJoin = 0
  FixShape = 1
  InnerFit = 0
  InnerFitJoin = 0
  InvalidShape = false
  Length = 8
  Length2 = 5
  NewSolid = false
  Placement = pos=(0,0,0) rot=(0.57735,0.57735,0.57735;2.0944rad)
  Profile = -> Sketch226
  ReferenceAxis = -> Sketch226 [N_Axis]
  Refine = true
  Suppress = false
  TaperInnerAngle = 0
  TaperInnerAngleRev = 0
  TreeRank = 0
  Type = 0
  ValidateShape = true
  _ProfileBasedVersion = 0
  _Version = 0
FEATURE [Sketcher::SketchObject] Sketch227
  ArcFitTolerance = 0
  AttachmentSupport = -> [Pocket069]
  ExternalBSplineMaxDegree = 0
  ExternalBSplineTolerance = 0
  FixShape = 1
  FullyConstrained = true
  InternalTolerance = 1e-06
  InvalidShape = false
  MakeInternals = false
  MapMode = 5
  Placement = pos=(5,1.02e-14,-4.9e-15) rot=(0.57735,0.57735,0.57735;2.0944rad)
  Support = -> [Pocket069]
  TreeRank = 0
  ValidateShape = false
  sketch-geometry (1):
    g0: Circle CenterX=0 CenterY=0 CenterZ=0 NormalX=0 NormalY=0 NormalZ=1 AngleXU=0 Radius=3.2
  constraints (2):
    c: Coincident(g0,g-1)
    c: Diameter(g0) = 6.4
FEATURE [PartDesign::Pocket] Pocket070
  AddSubType = 1
  AutoTaperInnerAngle = true
  BaseFeature = -> Pocket069
  CheckUpToFaceLimits = true
  ClaimChildren = false
  Direction = (-1,-1.9e-15,8e-16)
  Fit = 0
  FitJoin = 0
  FixShape = 1
  InnerFit = 0
  InnerFitJoin = 0
  InvalidShape = false
  Length = 8
  Length2 = 5
  NewSolid = false
  Placement = pos=(0,0,0) rot=(0.57735,0.57735,0.57735;2.0944rad)
  Profile = -> Sketch227
  ReferenceAxis = -> Sketch227 [N_Axis]
  Refine = true
  Suppress = false
  TaperInnerAngle = 0
  TaperInnerAngleRev = 0
  TreeRank = 0
  Type = 0
  ValidateShape = true
  _ProfileBasedVersion = 0
  _Version = 0
FEATURE [Sketcher::SketchObject] Sketch228
  ArcFitTolerance = 0
  ExternalBSplineMaxDegree = 0
  ExternalBSplineTolerance = 0
  ExternalGeometry = -> [Pocket070]
  FixShape = 1
  FullyConstrained = true
  InternalTolerance = 1e-06
  InvalidShape = false
  MakeInternals = false
  MapMode = 5
  Placement = pos=(0,0,0) rot=(0.57735,0.57735,0.57735;2.0944rad)
  TreeRank = 0
  ValidateShape = false
  sketch-geometry (5):
    g0: LineSegment StartX=-1.5 StartY=-5 StartZ=0 EndX=-1.5 EndY=-4.7 EndZ=0
    g1: LineSegment StartX=-1.5 StartY=-4.7 StartZ=0 EndX=-3.2 EndY=-3 EndZ=0
    g2: LineSegment StartX=-3.2 StartY=-3 StartZ=0 EndX=0 EndY=-3 EndZ=0
    g3: LineSegment StartX=0 StartY=-3 StartZ=0 EndX=0 EndY=-5 EndZ=0
    g4: LineSegment StartX=0 StartY=-5 StartZ=0 EndX=-1.5 EndY=-5 EndZ=0
  constraints (13):
    c: Coincident(g0,g-3)
    c: Coincident(g1,g0)
    c: PointOnObject(g2,g-2)
    c: Horizontal(g2)
    c: Coincident(g3,g2)
    c: PointOnObject(g3,g-3)
    c: Vertical(g3)
    c: Coincident(g4,g3)
    c: Coincident(g4,g0)
    c: Vertical(g0)
    c: Coincident(g1,g2)
    c: Angle(g1,g2) = 0.785398
    c: Coincident(g1,g-4)
FEATURE [PartDesign::Groove] Groove003
  AddSubType = 1
  Angle = 360
  Axis = (1e-16,1e-16,1)
  Base = (0,0,0)
  BaseFeature = -> Pocket070
  ClaimChildren = false
  Fit = 0
  FitJoin = 0
  FixShape = 1
  InnerFit = 0
  InnerFitJoin = 0
  InvalidShape = false
  NewSolid = false
  Placement = pos=(0,0,0) rot=(0.57735,0.57735,0.57735;2.0944rad)
  Profile = -> Sketch228
  ReferenceAxis = -> Z_Axis132
  Refine = true
  Reversed = true
  Suppress = false
  TreeRank = 0
  ValidateShape = true
  _ProfileBasedVersion = 0
FEATURE [PartDesign::PolarPattern] PolarPattern024
  AddSubType = 0
  Angle = 90
  Axis = -> Y_Axis132
  BaseFeature = -> Groove003
  CopyShape = true
  FixShape = 1
  InvalidShape = false
  NewSolid = false
  Occurrences = 2
  OriginalSubs = -> [Groove003]
  Originals = -> [Groove003]
  ParallelTransform = true
  Placement = pos=(0,0,0) rot=(0.57735,0.57735,0.57735;2.0944rad)
  Refine = true
  SubTransform = true
  Suppress = false
  TreeRank = 0
  ValidateShape = true
  _Version = 0
FEATURE [PartDesign::Chamfer] Chamfer049
  AddSubType = 0
  Angle = 45
  Base = -> PolarPattern024 [Edge11,Edge6,Edge1,Edge2]
  BaseFeature = -> PolarPattern024
  ChamferType = 0
  FixShape = 1
  FlipDirection = false
  InvalidShape = false
  NewSolid = false
  Placement = pos=(0,0,0) rot=(0.57735,0.57735,0.57735;2.0944rad)
  Refine = true
  Size = 1
  Size2 = 1
  SupportTransform = false
  Suppress = false
  TreeRank = 0
  UseAllEdges = false
  ValidateShape = true
FEATURE [Sketcher::SketchObject] Sketch229
  ArcFitTolerance = 0
  AttachmentSupport = -> [Chamfer049]
  ExternalBSplineMaxDegree = 0
  ExternalBSplineTolerance = 0
  ExternalGeometry = -> [Chamfer049]
  FixShape = 1
  FullyConstrained = true
  InternalTolerance = 1e-06
  InvalidShape = false
  MakeInternals = false
  MapMode = 5
  Placement = pos=(5,1.46e-14,-6.5e-15) rot=(0.57735,0.57735,0.57735;2.0944rad)
  Support = -> [Chamfer049]
  TreeRank = 0
  ValidateShape = false
  sketch-geometry (11):
    g0: LineSegment StartX=23.2045 StartY=-10.8358 StartZ=0 EndX=20.5858 EndY=4.01519 EndZ=0
    g1: LineSegment StartX=20.5858 StartY=4.01519 StartZ=0 EndX=19.4122 EndY=5 EndZ=0
    g2: LineSegment StartX=19.4122 StartY=5 StartZ=0 EndX=-4 EndY=5 EndZ=0
    g3: LineSegment StartX=-4 StartY=5 StartZ=0 EndX=-5 EndY=4 EndZ=0
    g4: LineSegment StartX=-5 StartY=4 StartZ=0 EndX=-5 EndY=-13.3034 EndZ=0
    g5: LineSegment StartX=-5 StartY=-13.3034 StartZ=0 EndX=23.2045 EndY=-10.8358 EndZ=0
    g6: LineSegment [constr] StartX=23.2045 StartY=-10.8358 StartZ=0 EndX=-5 EndY=-10.8358 EndZ=0
    g7: LineSegment [constr] StartX=-5 StartY=-13.3034 StartZ=0 EndX=22.776 EndY=-8.40576 EndZ=0
    g8: LineSegment [constr] StartX=22.776 StartY=-8.40576 StartZ=0 EndX=23.2045 EndY=-10.8358 EndZ=0
    g9: LineSegment [constr] StartX=-5 StartY=-10.8358 StartZ=0 EndX=-5 EndY=-13.3034 EndZ=0
    g10: Circle CenterX=0 CenterY=0 CenterZ=0 NormalX=0 NormalY=0 NormalZ=1 AngleXU=0 Radius=3
  constraints (26):
    c: Coincident(g0,g-4)
    c: Coincident(g0,g1)
    c: Coincident(g1,g-5)
    c: Coincident(g1,g2)
    c: Coincident(g2,g-6)
    c: Coincident(g2,g3)
    c: Coincident(g3,g-7)
    c: Coincident(g3,g4)
    c: Vertical(g4)
    c: Coincident(g4,g5)
    c: Coincident(g5,g0)
    c: PointOnObject(g-3,g0)
    c: Coincident(g0,g6)
    c: PointOnObject(g6,g4)
    c: Horizontal(g6)
    c: Coincident(g4,g7)
    c: PointOnObject(g7,g0)
    c: Perpendicular(g7,g0)
    c: Coincident(g7,g8)
    c: Coincident(g8,g0)
    c: Coincident(g6,g9)
    c: Coincident(g9,g4)
    c: Equal(g8,g9)
    c: DistanceY(g0,g-3) = 5
    c: Coincident(g10,g-1)
    c: Diameter(g10) = 6
FEATURE [PartDesign::Pad] Pad092
  AddSubType = 0
  AutoTaperInnerAngle = true
  BaseFeature = -> Chamfer049
  CheckUpToFaceLimits = true
  ClaimChildren = false
  Direction = (1,2.8e-15,-1.3e-15)
  Fit = 0
  FitJoin = 0
  FixShape = 1
  InnerFit = 0
  InnerFitJoin = 0
  InvalidShape = false
  Length = 3
  Length2 = 10
  NewSolid = false
  Placement = pos=(0,0,0) rot=(0.57735,0.57735,0.57735;2.0944rad)
  Profile = -> Sketch229
  ReferenceAxis = -> Sketch229 [N_Axis]
  Refine = true
  Suppress = false
  TaperInnerAngle = 0
  TaperInnerAngleRev = 0
  TreeRank = 0
  Type = 0
  ValidateShape = true
  _ProfileBasedVersion = 0
FEATURE [PartDesign::Chamfer] Chamfer050
  AddSubType = 0
  Angle = 45
  Base = -> Pad092 [Edge53,Edge52]
  BaseFeature = -> Pad092
  ChamferType = 0
  FixShape = 1
  FlipDirection = false
  InvalidShape = false
  NewSolid = false
  Placement = pos=(0,0,0) rot=(0.57735,0.57735,0.57735;2.0944rad)
  Refine = true
  Size = 1
  Size2 = 1
  SupportTransform = false
  Suppress = false
  TreeRank = 0
  UseAllEdges = false
  ValidateShape = true
FEATURE [Sketcher::SketchObject] Sketch238
  ArcFitTolerance = 1e-06
  AttachmentSupport = -> [Chamfer050]
  ExternalBSplineMaxDegree = 5
  ExternalBSplineTolerance = 0.0001
  FixShape = 1
  FullyConstrained = true
  InternalTolerance = 1e-06
  InvalidShape = false
  MakeInternals = false
  MapMode = 5
  Placement = pos=(8,2.66e-14,-1.16e-14) rot=(0.57735,0.57735,0.57735;2.0944rad)
  Support = -> [Chamfer050]
  TreeRank = 1
  ValidateShape = false
  sketch-geometry (1):
    g0: Circle CenterX=8 CenterY=0 CenterZ=0 NormalX=0 NormalY=0 NormalZ=1 AngleXU=0 Radius=1.6
  constraints (3):
    c: PointOnObject(g0,g-1)
    c: Diameter(g0) = 3.2
    c: DistanceX(g-1,g0) = 8
FEATURE [PartDesign::Pocket] Pocket078
  AddSubType = 1
  AlongSketchNormal = false
  AutoTaperInnerAngle = true
  BaseFeature = -> Chamfer050
  CheckUpToFaceLimits = true
  ClaimChildren = false
  Direction = (-1,-3.2e-15,1.4e-15)
  Fit = 0
  FitJoin = 0
  FixShape = 1
  InnerFit = 0
  InnerFitJoin = 0
  InvalidShape = false
  Length = 5
  Length2 = 10
  Linearize = true
  NewSolid = false
  Profile = -> Sketch238
  ReferenceAxis = -> Sketch238 [N_Axis]
  Refine = true
  Suppress = false
  TaperInnerAngle = 0
  TaperInnerAngleRev = 0
  TreeRank = 2
  Type = 1
  ValidateShape = true
  _ProfileBasedVersion = 1
  _Version = 1
FEATURE [Sketcher::SketchObject] Sketch239
  ArcFitTolerance = 1e-06
  AttachmentSupport = -> [Pocket078]
  ExternalBSplineMaxDegree = 5
  ExternalBSplineTolerance = 0.0001
  ExternalGeometry = -> [Pocket078]
  FixShape = 1
  FullyConstrained = true
  InternalTolerance = 1e-06
  InvalidShape = false
  MakeInternals = false
  MapMode = 5
  Placement = pos=(-5,-1.54e-14,7.3e-15) rot=(0.57735,-0.57735,-0.57735;2.0944rad)
  Support = -> [Pocket078]
  TreeRank = 3
  ValidateShape = false
  sketch-geometry (7):
    g0: LineSegment StartX=-4.82457 StartY=0 StartZ=0 EndX=-6.41229 EndY=2.75 EndZ=0
    g1: LineSegment StartX=-6.41229 StartY=2.75 StartZ=0 EndX=-9.58771 EndY=2.75 EndZ=0
    g2: LineSegment StartX=-9.58771 StartY=2.75 StartZ=0 EndX=-11.1754 EndY=-1.51e-14 EndZ=0
    g3: LineSegment StartX=-11.1754 StartY=-1.5e-14 StartZ=0 EndX=-9.58771 EndY=-2.75 EndZ=0
    g4: LineSegment StartX=-9.58771 StartY=-2.75 StartZ=0 EndX=-6.41229 EndY=-2.75 EndZ=0
    g5: LineSegment StartX=-6.41229 StartY=-2.75 StartZ=0 EndX=-4.82457 EndY=0 EndZ=0
    g6: Circle [constr] CenterX=-8 CenterY=-4e-16 CenterZ=0 NormalX=0 NormalY=0 NormalZ=1 AngleXU=0 Radius=3.17543
  constraints (16):
    c: Coincident(g0,g1)
    c: Coincident(g1,g2)
    c: Coincident(g2,g3)
    c: Coincident(g3,g4)
    c: Coincident(g4,g5)
    c: Coincident(g5,g0)
    c: Equal(g0, g1-g5) x5
    c: PointOnObject(g0,g6)
    c: PointOnObject(g1,g6)
    c: PointOnObject(g2,g6)
    c: PointOnObject(g3,g6)
    c: PointOnObject(g4,g6)
    c: PointOnObject(g5,g6)
    c: Coincident(g6,g-3)
    c: PointOnObject(g5,g-1)
    c: DistanceY(g3,g1) = 5.5
FEATURE [PartDesign::Pocket] Pocket079
  AddSubType = 1
  AlongSketchNormal = false
  AutoTaperInnerAngle = true
  BaseFeature = -> Pocket078
  CheckUpToFaceLimits = true
  ClaimChildren = false
  Direction = (1,3e-15,-1.4e-15)
  Fit = 0
  FitJoin = 0
  FixShape = 1
  InnerFit = 0
  InnerFitJoin = 0
  InvalidShape = false
  Length = 5
  Length2 = 10
  Linearize = true
  NewSolid = false
  Profile = -> Sketch239
  ReferenceAxis = -> Sketch239 [N_Axis]
  Refine = true
  Suppress = false
  TaperInnerAngle = 0
  TaperInnerAngleRev = 0
  TreeRank = 4
  Type = 0
  ValidateShape = true
  _ProfileBasedVersion = 1
  _Version = 1
FEATURE [PartDesign::Chamfer] Chamfer056
  AddSubType = 0
  Angle = 45
  Base = -> Pocket079 [Face12,Edge66,Edge49,Edge50,Edge51,Edge52,Edge53,Edge48,Edge28,Edge35,Edge37,Edge31,Edge26,Edge20,Edge43,Edge44,Edge45,Edge24]
  BaseFeature = -> Pocket079
  ChamferType = 0
  FixShape = 1
  FlipDirection = false
  InvalidShape = false
  NewSolid = false
  Refine = true
  Size = 0.4
  Size2 = 1
  SupportTransform = false
  Suppress = false
  TreeRank = 5
  UseAllEdges = false
  ValidateShape = true
FEATURE [PartDesign::Body] Body108  label="Link_100_deg"
  AutoGroupSolids = false
  ClaimAllChildren = false
  ExportMode = 0
  FixShape = 1
  Group = -> [Sketch221,Pad090,Sketch222,Pocket067,Sketch223,Pocket068,Sketch224,Pad091,Sketch225,Groove002,Sketch226,Pocket069,Sketch227,Pocket070,Sketch228,Groove003,PolarPattern024,Chamfer049,Sketch229,Pad092,Chamfer050,Sketch238,Pocket078,Sketch239,Pocket079,Chamfer056]
  InvalidShape = false
  Origin = -> Origin209
  SingleSolid = true
  Tip = -> Chamfer056
  TreeRank = 0
  ValidateShape = false
  _ExportChildren = -> [Pad090,Pocket067,Pocket068,Pad091,Groove002,Pocket069,Pocket070,Groove003,PolarPattern024,Chamfer049,Pad092,Chamfer050,Pocket078,Pocket079,Chamfer056]
  _GroupVersion = 1
COMPONENT P11 — geometry summary ("Link_100_deg_Clone"; no construction recipe available for this part):
  bounding box: 28.0 x 18.2 x 13.0 mm
  tessellated surface: 6,100 triangles
  volume: 3153 mm^3 (47% of its bounding box)
COMPONENT P12 — recipe-attached ("FlatMagnet - 60x13,5x5 mm - 30kg", modeled in this document).
Construction recipe (the document's own serialized feature program — sketch geometry with constraints, then the solid features built on it; lengths are millimeters unless a unit is written):

FEATURE [Sketcher::SketchObject] Sketch250
  ArcFitTolerance = 1e-06
  AttachmentSupport = -> [XZ_Plane142]
  ExternalBSplineMaxDegree = 5
  ExternalBSplineTolerance = 0.0001
  FixShape = 1
  FullyConstrained = true
  InternalTolerance = 1e-06
  InvalidShape = false
  MakeInternals = false
  MapMode = 5
  Placement = pos=(0,0,0) rot=(1,0,0;1.5708rad)
  Support = -> [XZ_Plane142]
  TreeRank = 59
  ValidateShape = false
  sketch-geometry (7):
    g0: LineSegment StartX=-4.7 StartY=-30 StartZ=0 EndX=-4.7 EndY=30 EndZ=0
    g1: LineSegment StartX=-4.7 StartY=30 StartZ=0 EndX=4.7 EndY=30 EndZ=0
    g2: LineSegment StartX=4.7 StartY=30 StartZ=0 EndX=4.7 EndY=-30 EndZ=0
    g3: LineSegment StartX=4.7 StartY=-30 StartZ=0 EndX=-4.7 EndY=-30 EndZ=0
    g4: GeomPoint [constr] X=0 Y=0 Z=0
    g5: Circle CenterX=0 CenterY=23.5 CenterZ=0 NormalX=0 NormalY=0 NormalZ=1 AngleXU=0 Radius=1.5
    g6: Circle CenterX=0 CenterY=-23.5 CenterZ=0 NormalX=0 NormalY=0 NormalZ=1 AngleXU=0 Radius=1.5
  constraints (17):
    c: Coincident(g0,g1)
    c: Coincident(g1,g2)
    c: Coincident(g2,g3)
    c: Coincident(g3,g0)
    c: Horizontal(g1)
    c: Horizontal(g3)
    c: Vertical(g0)
    c: Vertical(g2)
    c: Symmetric(g1,g0,g4)
    c: Coincident(g4,g-1)
    c: PointOnObject(g5,g-2)
    c: Symmetric(g5,g6,g4)
    c: DistanceY(g6,g5) = 47
    c: DistanceY(g2,g2) = 60
    c: DistanceX(g1,g1) = 9.4
    c: Equal(g5,g6)
    c: Diameter(g5) = 3
FEATURE [PartDesign::Pad] Pad100
  AddSubType = 0
  AlongSketchNormal = false
  AutoTaperInnerAngle = true
  CheckUpToFaceLimits = true
  ClaimChildren = false
  Direction = (0,-1,2e-16)
  Fit = 0
  FitJoin = 0
  FixShape = 1
  InnerFit = 0
  InnerFitJoin = 0
  InvalidShape = false
  Length = 3
  Length2 = 10
  Linearize = true
  NewSolid = false
  Profile = -> Sketch250
  ReferenceAxis = -> Sketch250 [N_Axis]
  Refine = true
  Suppress = false
  TaperInnerAngle = 0
  TaperInnerAngleRev = 0
  TreeRank = 60
  Type = 0
  ValidateShape = true
  _ProfileBasedVersion = 1
FEATURE [PartDesign::Chamfer] Chamfer057
  AddSubType = 0
  Angle = 45
  Base = -> Pad100 [Edge15,Edge18]
  BaseFeature = -> Pad100
  ChamferType = 0
  FixShape = 1
  FlipDirection = false
  InvalidShape = false
  NewSolid = false
  Refine = true
  Size = 2
  Size2 = 1
  SupportTransform = false
  Suppress = false
  TreeRank = 61
  UseAllEdges = false
  ValidateShape = true
FEATURE [PartDesign::Fillet] Fillet047
  AddSubType = 0
  Base = -> Chamfer057 [Edge17,Edge18,Edge16,Edge19]
  BaseFeature = -> Chamfer057
  FixShape = 1
  InvalidShape = false
  NewSolid = false
  Radius = 1
  Refine = true
  SupportTransform = false
  Suppress = false
  TreeRank = 62
  UseAllEdges = false
  ValidateShape = true
FEATURE [PartDesign::Fillet] Fillet048
  AddSubType = 0
  Base = -> Fillet047 [Edge13,Edge1]
  BaseFeature = -> Fillet047
  FixShape = 1
  InvalidShape = false
  NewSolid = false
  Radius = 0.4
  Refine = true
  SupportTransform = false
  Suppress = false
  TreeRank = 63
  UseAllEdges = false
  ValidateShape = true
FEATURE [PartDesign::Body] Body116  label="FlatMagnet - 60x13,5x5 mm - 30kg"
  AutoGroupSolids = false
  ClaimAllChildren = false
  ExportMode = 0
  FixShape = 1
  Group = -> [Sketch250,Pad100,Chamfer057,Fillet047,Fillet048]
  InvalidShape = false
  Origin = -> Origin219
  SingleSolid = true
  Tip = -> Fillet048
  TreeRank = 58
  ValidateShape = false
  _ExportChildren = -> [Pad100,Chamfer057,Fillet047,Fillet048]
  _GroupVersion = 1
COMPONENT P13 — recipe-attached ("SuctionCupDP15mm", modeled in this document).
Construction recipe (the document's own serialized feature program — sketch geometry with constraints, then the solid features built on it; lengths are millimeters unless a unit is written):

FEATURE [Sketcher::SketchObject] Sketch265
  ArcFitTolerance = 1e-06
  AttachmentSupport = -> [XZ_Plane151]
  ExternalBSplineMaxDegree = 5
  ExternalBSplineTolerance = 0.0001
  FixShape = 1
  FullyConstrained = true
  InternalTolerance = 1e-06
  InvalidShape = false
  MakeInternals = false
  MapMode = 5
  Placement = pos=(0,0,0) rot=(1,0,0;1.5708rad)
  Support = -> [XZ_Plane151]
  TreeRank = 207
  ValidateShape = false
  sketch-geometry (9):
    g0: LineSegment StartX=7.5 StartY=0 StartZ=0 EndX=7.5 EndY=-7 EndZ=0
    g1: LineSegment StartX=7.5 StartY=-7 StartZ=0 EndX=5.25 EndY=-8.5 EndZ=0
    g2: LineSegment StartX=5.25 StartY=-8.5 StartZ=0 EndX=2 EndY=-8.5 EndZ=0
    g3: LineSegment StartX=2 StartY=-8.5 StartZ=0 EndX=2 EndY=-5.4 EndZ=0
    g4: LineSegment StartX=2 StartY=-5.4 StartZ=0 EndX=3.5 EndY=-5.4 EndZ=0
    g5: LineSegment StartX=3.5 StartY=-5.4 StartZ=0 EndX=3.5 EndY=-3 EndZ=0
    g6: LineSegment StartX=3.5 StartY=-3 StartZ=0 EndX=2.5 EndY=-3 EndZ=0
    g7: LineSegment StartX=2.5 StartY=-3 StartZ=0 EndX=2.5 EndY=0 EndZ=0
    g8: LineSegment StartX=2.5 StartY=0 StartZ=0 EndX=7.5 EndY=0 EndZ=0
  constraints (27):
    c: PointOnObject(g0,g-1)
    c: Vertical(g0)
    c: Coincident(g0,g1)
    c: Coincident(g2,g1)
    c: Horizontal(g2)
    c: Coincident(g2,g3)
    c: Vertical(g3)
    c: Coincident(g3,g4)
    c: Horizontal(g4)
    c: Coincident(g4,g5)
    c: Vertical(g5)
    c: Coincident(g5,g6)
    c: Horizontal(g6)
    c: Coincident(g6,g7)
    c: Vertical(g7)
    c: Coincident(g8,g7)
    c: Coincident(g8,g0)
    c: Horizontal(g8)
    c: DistanceX(g-1,g7) = 2.5
    c: DistanceY(g7,g7) = 3
    c: DistanceY(g4,g-1) = 5.4
    c: DistanceX(g-1,g5) = 3.5
    c: DistanceX(g-1,g0) = 7.5
    c: DistanceX(g-1,g2) = 2
    c: DistanceY(g1,g0) = 8.5
    c: DistanceX(g-1,g1) = 5.25
    c: DistanceY(g0,g0) = 7
FEATURE [PartDesign::Revolution] Revolution028
  AddSubType = 0
  Angle = 360
  Axis = (0,2e-16,1)
  Base = (0,0,0)
  ClaimChildren = false
  Fit = 0
  FitJoin = 0
  FixShape = 1
  InnerFit = 0
  InnerFitJoin = 0
  InvalidShape = false
  Linearize = true
  NewSolid = false
  Profile = -> Sketch265
  ReferenceAxis = -> Sketch265 [V_Axis]
  Refine = true
  Reversed = true
  Suppress = false
  TreeRank = 208
  ValidateShape = true
  _ProfileBasedVersion = 1
FEATURE [PartDesign::Fillet] Fillet054
  AddSubType = 0
  Base = -> Revolution028 [Edge1,Edge3]
  BaseFeature = -> Revolution028
  FixShape = 1
  InvalidShape = false
  NewSolid = false
  Radius = 1
  Refine = true
  SupportTransform = false
  Suppress = false
  TreeRank = 209
  UseAllEdges = false
  ValidateShape = true
FEATURE [Sketcher::SketchObject] Sketch266
  ArcFitTolerance = 1e-06
  AttachmentSupport = -> [XZ_Plane151]
  ExternalBSplineMaxDegree = 5
  ExternalBSplineTolerance = 0.0001
  ExternalGeometry = -> [Fillet054]
  FixShape = 1
  FullyConstrained = true
  InternalTolerance = 1e-06
  InvalidShape = false
  MakeInternals = false
  MapMode = 5
  Placement = pos=(0,0,0) rot=(1,0,0;1.5708rad)
  Support = -> [XZ_Plane151]
  TreeRank = 210
  ValidateShape = false
  sketch-geometry (12):
    g0: LineSegment StartX=5.25 StartY=-8.5 StartZ=0 EndX=8 EndY=-11.75 EndZ=0
    g1: LineSegment StartX=8 StartY=-11.75 StartZ=0 EndX=5.25 EndY=-15 EndZ=0
    g2: LineSegment StartX=5.25 StartY=-15 StartZ=0 EndX=8 EndY=-17.5 EndZ=0
    g3: LineSegment [constr] StartX=8 StartY=-17.5 StartZ=0 EndX=0 EndY=-17.5 EndZ=0
    g4: LineSegment [constr] StartX=0 StartY=-17.5 StartZ=0 EndX=0 EndY=-8.5 EndZ=0
    g5: LineSegment [constr] StartX=0 StartY=-8.5 StartZ=0 EndX=5.25 EndY=-8.5 EndZ=0
    g6: LineSegment StartX=5.25 StartY=-8.5 StartZ=0 EndX=2 EndY=-8.5 EndZ=0
    g7: LineSegment StartX=2 StartY=-8.5 StartZ=0 EndX=7.5 EndY=-11.75 EndZ=0
    g8: LineSegment StartX=7.5 StartY=-11.75 StartZ=0 EndX=4.75 EndY=-15 EndZ=0
    g9: LineSegment StartX=8 StartY=-17.5 StartZ=0 EndX=4.75 EndY=-15 EndZ=0
    g10: LineSegment [constr] StartX=7.5 StartY=-11.75 StartZ=0 EndX=8 EndY=-11.75 EndZ=0
    g11: LineSegment [constr] StartX=4.75 StartY=-15 StartZ=0 EndX=5.25 EndY=-15 EndZ=0
  constraints (31):
    c: Coincident(g-4,g0)
    c: Coincident(g0,g1)
    c: Coincident(g1,g2)
    c: Coincident(g2,g3)
    c: PointOnObject(g3,g-2)
    c: Horizontal(g3)
    c: Coincident(g3,g4)
    c: PointOnObject(g4,g-4)
    c: Vertical(g4)
    c: Coincident(g4,g5)
    c: Coincident(g5,g0)
    c: Coincident(g6,g0)
    c: Coincident(g6,g-3)
    c: Coincident(g7,g6)
    c: Coincident(g8,g7)
    c: Coincident(g9,g2)
    c: Coincident(g9,g8)
    c: DistanceX(g3,g3) = 8
    c: DistanceY(g3,g-1) = 17.5
    c: Vertical(g0,g2)
    c: Equal(g0,g1)
    c: DistanceY(g2,g1) = 2.5
    c: Vertical(g1,g0)
    c: Horizontal(g7,g0)
    c: Horizontal(g1,g8)
    c: Coincident(g10,g7)
    c: Coincident(g10,g0)
    c: Coincident(g11,g8)
    c: Coincident(g11,g1)
    c: Equal(g11,g10)
    c: DistanceX(g10,g10) = 0.5
FEATURE [PartDesign::Revolution] Revolution029
  AddSubType = 0
  Angle = 360
  Axis = (0,2e-16,1)
  Base = (0,0,0)
  BaseFeature = -> Fillet054
  ClaimChildren = false
  Fit = 0
  FitJoin = 0
  FixShape = 1
  InnerFit = 0
  InnerFitJoin = 0
  InvalidShape = false
  Linearize = true
  NewSolid = false
  Profile = -> Sketch266
  ReferenceAxis = -> Sketch266 [V_Axis]
  Refine = true
  Reversed = true
  Suppress = false
  TreeRank = 211
  ValidateShape = true
  _ProfileBasedVersion = 1
FEATURE [PartDesign::Fillet] Fillet055
  AddSubType = 0
  Base = -> Revolution029 [Edge14,Edge10,Edge17]
  BaseFeature = -> Revolution029
  FixShape = 1
  InvalidShape = false
  NewSolid = false
  Radius = 0.5
  Refine = true
  SupportTransform = false
  Suppress = false
  TreeRank = 212
  UseAllEdges = false
  ValidateShape = true
FEATURE [PartDesign::Body] Body125  label="SuctionCupDP15mm"
  AutoGroupSolids = false
  ClaimAllChildren = false
  ExportMode = 0
  FixShape = 1
  Group = -> [Sketch265,Revolution028,Fillet054,Sketch266,Revolution029,Fillet055]
  InvalidShape = false
  Origin = -> Origin230
  SingleSolid = true
  Tip = -> Fillet055
  TreeRank = 206
  ValidateShape = false
  _ExportChildren = -> [Revolution028,Fillet054,Revolution029,Fillet055]
  _GroupVersion = 1
COMPONENT P14 — recipe-attached ("Adaptator-suction-cup-spring-version", modeled in this document).
Construction recipe (the document's own serialized feature program — sketch geometry with constraints, then the solid features built on it; lengths are millimeters unless a unit is written):

FEATURE [Sketcher::SketchObject] Sketch267
  ArcFitTolerance = 1e-06
  AttachmentSupport = -> [XY_Plane152]
  ExternalBSplineMaxDegree = 5
  ExternalBSplineTolerance = 0.0001
  FixShape = 1
  FullyConstrained = true
  InternalTolerance = 1e-06
  InvalidShape = false
  MakeInternals = false
  MapMode = 5
  Support = -> [XY_Plane152]
  TreeRank = 148
  ValidateShape = false
  sketch-geometry (7):
    g0: LineSegment StartX=0 StartY=-6.9282 StartZ=0 EndX=6 EndY=-3.4641 EndZ=0
    g1: LineSegment StartX=6 StartY=-3.4641 StartZ=0 EndX=6 EndY=3.4641 EndZ=0
    g2: LineSegment StartX=6 StartY=3.4641 StartZ=0 EndX=0 EndY=6.9282 EndZ=0
    g3: LineSegment StartX=1e-16 StartY=6.9282 StartZ=0 EndX=-6 EndY=3.4641 EndZ=0
    g4: LineSegment StartX=-6 StartY=3.4641 StartZ=0 EndX=-6 EndY=-3.4641 EndZ=0
    g5: LineSegment StartX=-6 StartY=-3.4641 StartZ=0 EndX=0 EndY=-6.9282 EndZ=0
    g6: Circle [constr] CenterX=0 CenterY=0 CenterZ=0 NormalX=0 NormalY=0 NormalZ=1 AngleXU=0 Radius=6.9282
  constraints (16):
    c: Coincident(g0,g1)
    c: Coincident(g1,g2)
    c: Coincident(g2,g3)
    c: Coincident(g3,g4)
    c: Coincident(g4,g5)
    c: Coincident(g5,g0)
    c: Equal(g0, g1-g5) x5
    c: PointOnObject(g0,g6)
    c: PointOnObject(g1,g6)
    c: PointOnObject(g2,g6)
    c: PointOnObject(g3,g6)
    c: PointOnObject(g4,g6)
    c: PointOnObject(g5,g6)
    c: Coincident(g6,g-1)
    c: PointOnObject(g5,g-2)
    c: DistanceX(g3,g1) = 12
FEATURE [PartDesign::Pad] Pad106
  AddSubType = 0
  AlongSketchNormal = false
  AutoTaperInnerAngle = true
  CheckUpToFaceLimits = true
  ClaimChildren = false
  Direction = (0,0,1)
  Fit = 0
  FitJoin = 0
  FixShape = 1
  InnerFit = 0
  InnerFitJoin = 0
  InvalidShape = false
  Length = 8
  Length2 = 10
  Linearize = true
  NewSolid = false
  Profile = -> Sketch267
  ReferenceAxis = -> Sketch267 [N_Axis]
  Refine = true
  Suppress = false
  TaperInnerAngle = 0
  TaperInnerAngleRev = 0
  TreeRank = 149
  Type = 0
  ValidateShape = true
  _ProfileBasedVersion = 1
FEATURE [Sketcher::SketchObject] Sketch268
  ArcFitTolerance = 1e-06
  AttachmentSupport = -> [YZ_Plane152]
  ExternalBSplineMaxDegree = 5
  ExternalBSplineTolerance = 0.0001
  FixShape = 1
  FullyConstrained = true
  InternalTolerance = 1e-06
  InvalidShape = false
  MakeInternals = false
  MapMode = 5
  Placement = pos=(0,0,0) rot=(0.57735,0.57735,0.57735;2.0944rad)
  Support = -> [YZ_Plane152]
  TreeRank = 150
  ValidateShape = false
  sketch-geometry (6):
    g0: LineSegment StartX=0 StartY=0 StartZ=0 EndX=2.5 EndY=0 EndZ=0
    g1: LineSegment StartX=2.5 StartY=0 StartZ=0 EndX=2.5 EndY=-3 EndZ=0
    g2: LineSegment StartX=2.5 StartY=-3 StartZ=0 EndX=3.5 EndY=-3 EndZ=0
    g3: LineSegment StartX=3.5 StartY=-3 StartZ=0 EndX=3.5 EndY=-5.4 EndZ=0
    g4: LineSegment StartX=3.5 StartY=-5.4 StartZ=0 EndX=0 EndY=-5.4 EndZ=0
    g5: LineSegment StartX=0 StartY=-5.4 StartZ=0 EndX=0 EndY=0 EndZ=0
  constraints (17):
    c: Coincident(g-1,g0)
    c: PointOnObject(g0,g-1)
    c: Coincident(g0,g1)
    c: Vertical(g1)
    c: Coincident(g1,g2)
    c: Horizontal(g2)
    c: Coincident(g2,g3)
    c: Vertical(g3)
    c: Coincident(g3,g4)
    c: PointOnObject(g4,g-2)
    c: Horizontal(g4)
    c: Coincident(g4,g5)
    c: Coincident(g5,g0)
    c: DistanceX(g0,g0) = 2.5
    c: DistanceX(g4,g4) = 3.5
    c: DistanceY(g1,g1) = 3
    c: DistanceY(g3,g0) = 5.4
FEATURE [PartDesign::Revolution] Revolution030
  AddSubType = 0
  Angle = 360
  Axis = (-2e-16,3e-16,1)
  Base = (0,0,0)
  BaseFeature = -> Pad106
  ClaimChildren = false
  Fit = 0
  FitJoin = 0
  FixShape = 1
  InnerFit = 0
  InnerFitJoin = 0
  InvalidShape = false
  Linearize = true
  NewSolid = false
  Profile = -> Sketch268
  ReferenceAxis = -> Sketch268 [V_Axis]
  Refine = true
  Reversed = true
  Suppress = false
  TreeRank = 151
  ValidateShape = true
  _ProfileBasedVersion = 1
FEATURE [Sketcher::SketchObject] Sketch269
  ArcFitTolerance = 1e-06
  AttachmentSupport = -> [XZ_Plane152]
  ExternalBSplineMaxDegree = 5
  ExternalBSplineTolerance = 0.0001
  ExternalGeometry = -> [Revolution030]
  FixShape = 1
  FullyConstrained = true
  InternalTolerance = 1e-06
  InvalidShape = false
  MakeInternals = false
  MapMode = 5
  Placement = pos=(0,0,0) rot=(1,0,0;1.5708rad)
  Support = -> [XZ_Plane152]
  TreeRank = 152
  ValidateShape = false
  sketch-geometry (6):
    g0: LineSegment StartX=0 StartY=8 StartZ=0 EndX=0 EndY=38 EndZ=0
    g1: LineSegment StartX=0 StartY=38 StartZ=0 EndX=2.5 EndY=38 EndZ=0
    g2: LineSegment StartX=2.5 StartY=38 StartZ=0 EndX=2.5 EndY=12 EndZ=0
    g3: LineSegment StartX=2.5 StartY=12 StartZ=0 EndX=4 EndY=12 EndZ=0
    g4: LineSegment StartX=4 StartY=12 StartZ=0 EndX=4 EndY=8 EndZ=0
    g5: LineSegment StartX=4 StartY=8 StartZ=0 EndX=0 EndY=8 EndZ=0
  constraints (18):
    c: PointOnObject(g0,g-2)
    c: PointOnObject(g0,g-2)
    c: Coincident(g0,g1)
    c: Horizontal(g1)
    c: Coincident(g1,g2)
    c: Coincident(g2,g3)
    c: Horizontal(g3)
    c: Coincident(g3,g4)
    c: Vertical(g4)
    c: Coincident(g4,g5)
    c: Coincident(g5,g0)
    c: Horizontal(g5)
    c: Vertical(g2)
    c: PointOnObject(g4,g-3)
    c: DistanceX(g1,g1) = 2.5
    c: DistanceY(g0,g0) = 30
    c: DistanceY(g2,g2) = 26
    c: DistanceX(g0,g4) = 4
FEATURE [PartDesign::Revolution] Revolution031
  AddSubType = 0
  Angle = 360
  Axis = (0,-2e-16,1)
  Base = (0,0,0)
  BaseFeature = -> Revolution030
  ClaimChildren = false
  Fit = 0
  FitJoin = 0
  FixShape = 1
  InnerFit = 0
  InnerFitJoin = 0
  InvalidShape = false
  Linearize = true
  NewSolid = false
  Profile = -> Sketch269
  ReferenceAxis = -> Sketch269 [V_Axis]
  Refine = true
  Reversed = true
  Suppress = false
  TreeRank = 153
  ValidateShape = true
  _ProfileBasedVersion = 1
FEATURE [PartDesign::Chamfer] Chamfer063
  AddSubType = 0
  Angle = 45
  Base = -> Revolution031 [Edge26,Edge29]
  BaseFeature = -> Revolution031
  ChamferType = 0
  FixShape = 1
  FlipDirection = false
  InvalidShape = false
  NewSolid = false
  Refine = true
  Size = 0.2
  Size2 = 1
  SupportTransform = false
  Suppress = false
  TreeRank = 154
  UseAllEdges = false
  ValidateShape = true
FEATURE [Sketcher::SketchObject] Sketch270
  ArcFitTolerance = 1e-06
  AttachmentSupport = -> [Chamfer063]
  ExternalBSplineMaxDegree = 5
  ExternalBSplineTolerance = 0.0001
  FixShape = 1
  FullyConstrained = true
  InternalTolerance = 1e-06
  InvalidShape = false
  MakeInternals = false
  MapMode = 5
  Placement = pos=(1.2e-15,-1.5e-15,-5.4) rot=(1,0,0;3.14159rad)
  Support = -> [Chamfer063]
  TreeRank = 155
  ValidateShape = false
  sketch-geometry (1):
    g0: Circle CenterX=0 CenterY=0 CenterZ=0 NormalX=0 NormalY=0 NormalZ=1 AngleXU=0 Radius=1.5
  constraints (2):
    c: Coincident(g0,g-1)
    c: Diameter(g0) = 3
FEATURE [PartDesign::Pocket] Pocket089
  AddSubType = 1
  AlongSketchNormal = false
  AutoTaperInnerAngle = true
  BaseFeature = -> Chamfer063
  CheckUpToFaceLimits = true
  ClaimChildren = false
  Direction = (-2e-16,3e-16,1)
  Fit = 0
  FitJoin = 0
  FixShape = 1
  InnerFit = 0
  InnerFitJoin = 0
  InvalidShape = false
  Length = 12
  Length2 = 10
  Linearize = true
  NewSolid = false
  Profile = -> Sketch270
  ReferenceAxis = -> Sketch270 [N_Axis]
  Refine = true
  Suppress = false
  TaperInnerAngle = 0
  TaperInnerAngleRev = 0
  TreeRank = 156
  Type = 0
  ValidateShape = true
  _ProfileBasedVersion = 1
  _Version = 1
FEATURE [Sketcher::SketchObject] Sketch271
  ArcFitTolerance = 1e-06
  AttachmentSupport = -> [YZ_Plane152]
  ExternalBSplineMaxDegree = 5
  ExternalBSplineTolerance = 0.0001
  FixShape = 1
  FullyConstrained = true
  InternalTolerance = 1e-06
  InvalidShape = false
  MakeInternals = false
  MapMode = 5
  Placement = pos=(0,0,0) rot=(0.57735,0.57735,0.57735;2.0944rad)
  Support = -> [YZ_Plane152]
  TreeRank = 157
  ValidateShape = false
  sketch-geometry (1):
    g0: Circle CenterX=0 CenterY=4 CenterZ=0 NormalX=0 NormalY=0 NormalZ=1 AngleXU=0 Radius=2.5
  constraints (3):
    c: PointOnObject(g0,g-2)
    c: Diameter(g0) = 5
    c: DistanceY(g-1,g0) = 4
FEATURE [PartDesign::Pocket] Pocket090
  AddSubType = 1
  AlongSketchNormal = false
  AutoTaperInnerAngle = true
  BaseFeature = -> Pocket089
  CheckUpToFaceLimits = true
  ClaimChildren = false
  Direction = (-1,2e-16,-3e-16)
  Fit = 0
  FitJoin = 0
  FixShape = 1
  InnerFit = 0
  InnerFitJoin = 0
  InvalidShape = false
  Length = 5
  Length2 = 10
  Linearize = true
  Midplane = true
  NewSolid = false
  Profile = -> Sketch271
  ReferenceAxis = -> Sketch271 [N_Axis]
  Refine = true
  Suppress = false
  TaperInnerAngle = 0
  TaperInnerAngleRev = 0
  TreeRank = 158
  Type = 1
  ValidateShape = true
  _ProfileBasedVersion = 1
  _Version = 1
FEATURE [PartDesign::Chamfer] Chamfer064
  AddSubType = 0
  Angle = 45
  Base = -> Pocket090 [Edge24,Edge27]
  BaseFeature = -> Pocket090
  ChamferType = 0
  FixShape = 1
  FlipDirection = false
  InvalidShape = false
  NewSolid = false
  Refine = true
  Size = 0.2
  Size2 = 1
  SupportTransform = false
  Suppress = false
  TreeRank = 159
  UseAllEdges = false
  ValidateShape = true
FEATURE [PartDesign::Fillet] Fillet056
  AddSubType = 0
  Base = -> Chamfer064 [Edge2,Edge5,Edge8,Edge26,Edge28,Edge21]
  BaseFeature = -> Chamfer064
  FixShape = 1
  InvalidShape = false
  NewSolid = false
  Radius = 0.4
  Refine = true
  SupportTransform = false
  Suppress = false
  TreeRank = 160
  UseAllEdges = false
  ValidateShape = true
FEATURE [Sketcher::SketchObject] Sketch272
  ArcFitTolerance = 1e-06
  AttachmentSupport = -> [Fillet056]
  ExternalBSplineMaxDegree = 5
  ExternalBSplineTolerance = 0.0001
  FixShape = 1
  FullyConstrained = true
  InternalTolerance = 1e-06
  InvalidShape = false
  MakeInternals = false
  MapMode = 5
  Placement = pos=(0,-8.4e-15,38) rot=(0,0,1;0rad)
  Support = -> [Fillet056]
  TreeRank = 219
  ValidateShape = false
  sketch-geometry (1):
    g0: Circle CenterX=0 CenterY=0 CenterZ=0 NormalX=0 NormalY=0 NormalZ=1 AngleXU=0 Radius=1.5
  constraints (2):
    c: Coincident(g0,g-1)
    c: Diameter(g0) = 3
FEATURE [PartDesign::Pocket] Pocket091
  AddSubType = 1
  AlongSketchNormal = false
  AutoTaperInnerAngle = true
  BaseFeature = -> Fillet056
  CheckUpToFaceLimits = true
  ClaimChildren = false
  Direction = (0,2e-16,-1)
  Fit = 0
  FitJoin = 0
  FixShape = 1
  InnerFit = 0
  InnerFitJoin = 0
  InvalidShape = false
  Length = 8
  Length2 = 10
  Linearize = true
  NewSolid = false
  Profile = -> Sketch272
  ReferenceAxis = -> Sketch272 [N_Axis]
  Refine = true
  Suppress = false
  TaperInnerAngle = 0
  TaperInnerAngleRev = 0
  TreeRank = 220
  Type = 0
  ValidateShape = true
  _ProfileBasedVersion = 1
  _Version = 1
FEATURE [PartDesign::Chamfer] Chamfer065
  AddSubType = 0
  Angle = 45
  Base = -> Pocket091 [Edge66]
  BaseFeature = -> Pocket091
  ChamferType = 0
  FixShape = 1
  FlipDirection = false
  InvalidShape = false
  NewSolid = false
  Refine = true
  Size = 0.2
  Size2 = 1
  SupportTransform = false
  Suppress = false
  TreeRank = 221
  UseAllEdges = false
  ValidateShape = true
FEATURE [PartDesign::Body] Body126  label="Adaptator-suction-cup-spring-version"
  AutoGroupSolids = false
  ClaimAllChildren = false
  ExportMode = 0
  FixShape = 1
  Group = -> [Sketch267,Pad106,Sketch268,Revolution030,Sketch269,Revolution031,Chamfer063,Sketch270,Pocket089,Sketch271,Pocket090,Chamfer064,Fillet056,Sketch272,Pocket091,Chamfer065]
  InvalidShape = false
  Origin = -> Origin232
  SingleSolid = true
  Tip = -> Chamfer065
  TreeRank = 218
  ValidateShape = false
  _ExportChildren = -> [Pad106,Revolution030,Revolution031,Chamfer063,Pocket089,Pocket090,Chamfer064,Fillet056,Pocket091,Chamfer065]
  _GroupVersion = 1
COMPONENT P15 — recipe-attached ("OmniWheelAssembled", modeled in this document).
Construction recipe (the document's own serialized feature program — sketch geometry with constraints, then the solid features built on it; lengths are millimeters unless a unit is written):

FEATURE [Sketcher::SketchObject] Sketch245
  ArcFitTolerance = 0
  ExternalBSplineMaxDegree = 0
  ExternalBSplineTolerance = 0
  FixShape = 1
  FullyConstrained = true
  InternalTolerance = 1e-06
  InvalidShape = false
  MakeInternals = false
  MapMode = 5
  Placement = pos=(0,0,0) rot=(1,0,0;1.5708rad)
  TreeRank = 0
  ValidateShape = false
  sketch-geometry (1):
    g0: Circle CenterX=0 CenterY=0 CenterZ=0 NormalX=0 NormalY=0 NormalZ=1 AngleXU=0 Radius=13.9
  constraints (2):
    c: Coincident(g0,g-1)
    c: Diameter(g0) = 27.8
FEATURE [PartDesign::Pad] Pad098
  AddSubType = 0
  AutoTaperInnerAngle = true
  CheckUpToFaceLimits = true
  ClaimChildren = false
  Direction = (0,-1,2e-16)
  Fit = 0
  FitJoin = 0
  FixShape = 1
  InnerFit = 0
  InnerFitJoin = 0
  InvalidShape = false
  Length = 9
  Length2 = 10
  NewSolid = false
  Placement = pos=(0,0,0) rot=(1,0,0;1.5708rad)
  Profile = -> Sketch245
  ReferenceAxis = -> Sketch245 [N_Axis]
  Refine = true
  Reversed = true
  Suppress = false
  TaperInnerAngle = 0
  TaperInnerAngleRev = 0
  TreeRank = 0
  Type = 0
  ValidateShape = true
  _ProfileBasedVersion = 0
FEATURE [Sketcher::SketchObject] Sketch246
  ArcFitTolerance = 0
  AttachmentSupport = -> [Pad098]
  ExternalBSplineMaxDegree = 0
  ExternalBSplineTolerance = 0
  FixShape = 1
  FullyConstrained = true
  InternalTolerance = 1e-06
  InvalidShape = false
  MakeInternals = false
  MapMode = 5
  Placement = pos=(0,0,0) rot=(1,0,0;1.5708rad)
  Support = -> [Pad098]
  TreeRank = 0
  ValidateShape = false
  sketch-geometry (1):
    g0: Circle CenterX=0 CenterY=10.5 CenterZ=0 NormalX=0 NormalY=0 NormalZ=1 AngleXU=0 Radius=2.1
  constraints (3):
    c: PointOnObject(g0,g-2)
    c: DistanceY(g-1,g0) = 10.5
    c: Diameter(g0) = 4.2
FEATURE [Sketcher::SketchObject] Sketch247
  ArcFitTolerance = 0
  ExternalBSplineMaxDegree = 0
  ExternalBSplineTolerance = 0
  FixShape = 1
  FullyConstrained = true
  InternalTolerance = 1e-06
  InvalidShape = false
  MakeInternals = false
  MapMode = 5
  Placement = pos=(0,0,0) rot=(1,0,0;1.5708rad)
  TreeRank = 0
  ValidateShape = false
  sketch-geometry (1):
    g0: Circle CenterX=0 CenterY=0 CenterZ=0 NormalX=0 NormalY=0 NormalZ=1 AngleXU=0 Radius=2.5
  constraints (2):
    c: Coincident(g0,g-1)
    c: Diameter(g0) = 5
FEATURE [Sketcher::SketchObject] Sketch248
  ArcFitTolerance = 0
  ExternalBSplineMaxDegree = 0
  ExternalBSplineTolerance = 0
  FixShape = 1
  FullyConstrained = true
  InternalTolerance = 1e-06
  InvalidShape = false
  MakeInternals = false
  MapMode = 5
  Placement = pos=(0,0,0) rot=(1,0,0;1.5708rad)
  TreeRank = 0
  ValidateShape = false
  sketch-geometry (2):
    g0: LineSegment StartX=12.9696 StartY=5 StartZ=0 EndX=12.9696 EndY=-5 EndZ=0
    g1: ArcOfCircle CenterX=0 CenterY=0 CenterZ=0 NormalX=0 NormalY=0 NormalZ=1 AngleXU=0 Radius=13.9 StartAngle=5.91523 EndAngle=6.65114
  constraints (6):
    c: Vertical(g0)
    c: Coincident(g1,g-1)
    c: Coincident(g1,g0)
    c: Coincident(g1,g0)
    c: DistanceY(g0,g0) = 10
    c: Radius(g1) = 13.9
FEATURE [PartDesign::Hole] Hole001
  AddSubType = 1
  BaseFeature = -> Pad098
  ClaimChildren = false
  CustomThreadClearance = 0
  Depth = 81.4597
  DepthType = 1
  Diameter = 3.4
  DrillForDepth = false
  DrillPoint = 1
  DrillPointAngle = 118
  Fit = 0
  FitJoin = 0
  FixShape = 1
  HoleCutCountersinkAngle = 90
  HoleCutCustomValues = false
  HoleCutDepth = 0
  HoleCutDiameter = 6.1
  HoleCutType = 0
  InnerFit = 0
  InnerFitJoin = 0
  InvalidShape = false
  Linearize = true
  ModelThread = false
  NewSolid = false
  Profile = -> Sketch246
  Refine = true
  Suppress = false
  Tapered = false
  TaperedAngle = 90
  ThreadClass = 0
  ThreadDepth = 81.4597
  ThreadDepthType = 0
  ThreadDirection = 0
  ThreadFit = 0
  ThreadSize = 9
  ThreadType = 1
  Threaded = false
  TreeRank = 11
  UseCustomThreadClearance = false
  ValidateShape = true
  _ProfileBasedVersion = 1
FEATURE [PartDesign::PolarPattern] PolarPattern027
  AddSubType = 0
  Angle = 360
  Axis = -> Y_Axis140
  BaseFeature = -> Hole001
  CopyShape = true
  FixShape = 1
  InvalidShape = false
  NewSolid = false
  Occurrences = 6
  OriginalSubs = -> [Hole001]
  Originals = -> [Hole001]
  ParallelTransform = true
  Refine = true
  SubTransform = true
  Suppress = false
  TreeRank = 0
  ValidateShape = true
  _Version = 0
FEATURE [PartDesign::Pocket] Pocket085
  AddSubType = 1
  AutoTaperInnerAngle = true
  BaseFeature = -> PolarPattern027
  CheckUpToFaceLimits = true
  ClaimChildren = false
  Direction = (0,1,-2e-16)
  Fit = 0
  FitJoin = 0
  FixShape = 1
  InnerFit = 0
  InnerFitJoin = 0
  InvalidShape = false
  Length = 5
  Length2 = 5
  NewSolid = false
  Profile = -> Sketch247
  ReferenceAxis = -> Sketch247 [N_Axis]
  Refine = true
  Suppress = false
  TaperInnerAngle = 0
  TaperInnerAngleRev = 0
  TreeRank = 0
  Type = 1
  ValidateShape = true
  _ProfileBasedVersion = 0
  _Version = 0
FEATURE [PartDesign::Pocket] Pocket086
  AddSubType = 1
  AutoTaperInnerAngle = true
  BaseFeature = -> Pocket085
  CheckUpToFaceLimits = true
  ClaimChildren = false
  Direction = (0,1,-2e-16)
  Fit = 0
  FitJoin = 0
  FixShape = 1
  InnerFit = 0
  InnerFitJoin = 0
  InvalidShape = false
  Length = 5
  Length2 = 5
  NewSolid = false
  Profile = -> Sketch248
  ReferenceAxis = -> Sketch248 [N_Axis]
  Refine = true
  Suppress = false
  TaperInnerAngle = 0
  TaperInnerAngleRev = 0
  TreeRank = 0
  Type = 1
  ValidateShape = true
  _ProfileBasedVersion = 0
  _Version = 0
FEATURE [Sketcher::SketchObject] Sketch249
  ArcFitTolerance = 0
  AttachmentSupport = -> [Pocket086]
  ExternalBSplineMaxDegree = 0
  ExternalBSplineTolerance = 0
  ExternalGeometry = -> [Pocket086]
  FixShape = 1
  FullyConstrained = true
  InternalTolerance = 1e-06
  InvalidShape = false
  MakeInternals = false
  MapMode = 5
  Placement = pos=(12.9696,0,0) rot=(0.57735,0.57735,0.57735;2.0944rad)
  Support = -> [Pocket086]
  TreeRank = 0
  ValidateShape = false
  sketch-geometry (2):
    g0: Circle CenterX=4.5 CenterY=0 CenterZ=0 NormalX=0 NormalY=0 NormalZ=1 AngleXU=0 Radius=2.1
    g1: LineSegment [constr] StartX=9 StartY=0 StartZ=0 EndX=0 EndY=0 EndZ=0
  constraints (5):
    c: Diameter(g0) = 4.2
    c: Coincident(g1,g-1)
    c: Symmetric(g1,g1,g0)
    c: PointOnObject(g1,g-3)
    c: PointOnObject(g1,g-1)
FEATURE [PartDesign::Hole] Hole
  AddSubType = 1
  BaseFeature = -> Pocket086
  ClaimChildren = false
  CustomThreadClearance = 0
  Depth = 13
  DepthType = 0
  Diameter = 3.4
  DrillForDepth = false
  DrillPoint = 1
  DrillPointAngle = 118
  Fit = 0
  FitJoin = 0
  FixShape = 1
  HoleCutCountersinkAngle = 90
  HoleCutCustomValues = false
  HoleCutDepth = 0
  HoleCutDiameter = 6.1
  HoleCutType = 0
  InnerFit = 0
  InnerFitJoin = 0
  InvalidShape = false
  Linearize = true
  ModelThread = false
  NewSolid = false
  Profile = -> Sketch249
  Refine = true
  Suppress = false
  Tapered = false
  TaperedAngle = 90
  ThreadClass = 0
  ThreadDepth = 13
  ThreadDepthType = 0
  ThreadDirection = 0
  ThreadFit = 0
  ThreadSize = 9
  ThreadType = 1
  Threaded = false
  TreeRank = 10
  UseCustomThreadClearance = false
  ValidateShape = true
  _ProfileBasedVersion = 1
FEATURE [PartDesign::Body] Body114  label="NoyauRoueCNC"
  AutoGroupSolids = false
  ClaimAllChildren = false
  ExportMode = 0
  FixShape = 1
  Group = -> [Sketch245,Pad098,Sketch246,Hole001,PolarPattern027,Sketch247,Pocket085,Sketch248,Pocket086,Sketch249,Hole]
  InvalidShape = false
  Origin = -> Origin217
  Placement = pos=(3e-15,1.25,0) rot=(0,0,1;0rad)
  SingleSolid = true
  Tip = -> Hole
  TreeRank = 9
  ValidateShape = false
  _ExportChildren = -> [Pad098,Hole001,PolarPattern027,Pocket085,Pocket086,Hole]
  _GroupVersion = 1
COMPONENT P16 — recipe-attached ("MR148", modeled in this document).
Construction recipe (the document's own serialized feature program — sketch geometry with constraints, then the solid features built on it; lengths are millimeters unless a unit is written):

FEATURE [Sketcher::SketchObject] Sketch118
  ArcFitTolerance = 0
  ExternalBSplineMaxDegree = 0
  ExternalBSplineTolerance = 0
  FixShape = 1
  FullyConstrained = true
  InternalTolerance = 1e-06
  InvalidShape = false
  MakeInternals = false
  MapMode = 5
  Placement = pos=(0,0,0) rot=(1,0,0;1.5708rad)
  TreeRank = 0
  ValidateShape = false
  sketch-geometry (12):
    g0: LineSegment StartX=-6 StartY=2.67e-14 StartZ=0 EndX=-7 EndY=-1.177e-13 EndZ=0
    g1: LineSegment StartX=-7 StartY=-1.177e-13 StartZ=0 EndX=-7 EndY=4 EndZ=0
    g2: LineSegment StartX=-7 StartY=4 StartZ=0 EndX=-6 EndY=4 EndZ=0
    g3: LineSegment StartX=-6 StartY=4 StartZ=0 EndX=-6 EndY=3.6 EndZ=0
    g4: LineSegment StartX=-6 StartY=3.6 StartZ=0 EndX=-5 EndY=3.6 EndZ=0
    g5: LineSegment StartX=-5 StartY=3.6 StartZ=0 EndX=-5 EndY=4 EndZ=0
    g6: LineSegment StartX=-5 StartY=4 StartZ=0 EndX=-4 EndY=4 EndZ=0
    g7: LineSegment StartX=-4 StartY=4 StartZ=0 EndX=-4 EndY=0 EndZ=0
    g8: LineSegment StartX=-4 StartY=0 StartZ=0 EndX=-5 EndY=0 EndZ=0
    g9: LineSegment StartX=-5 StartY=0 StartZ=0 EndX=-5 EndY=0.4 EndZ=0
    g10: LineSegment StartX=-5 StartY=0.4 StartZ=0 EndX=-6 EndY=0.4 EndZ=0
    g11: LineSegment StartX=-6 StartY=0.4 StartZ=0 EndX=-6 EndY=2.67e-14 EndZ=0
  constraints (36):
    c: PointOnObject(g0,g-1)
    c: PointOnObject(g0,g-1)
    c: Coincident(g0,g1)
    c: Vertical(g1)
    c: Coincident(g1,g2)
    c: Horizontal(g2)
    c: Coincident(g2,g3)
    c: Vertical(g3)
    c: Coincident(g3,g4)
    c: Horizontal(g4)
    c: Coincident(g4,g5)
    c: Vertical(g5)
    c: Coincident(g5,g6)
    c: Horizontal(g6)
    c: Coincident(g6,g7)
    c: PointOnObject(g7,g-1)
    c: Vertical(g7)
    c: Coincident(g7,g8)
    c: PointOnObject(g8,g-1)
    c: Coincident(g8,g9)
    c: Vertical(g9)
    c: Coincident(g9,g10)
    c: Horizontal(g10)
    c: Coincident(g10,g11)
    c: Coincident(g11,g0)
    c: Vertical(g11)
    c: DistanceX(g7) = -4
    c: DistanceX(g0) = -7
    c: Equal(g8,g0)
    c: Equal(g2,g6)
    c: Equal(g4,g10)
    c: Equal(g3,g11)
    c: DistanceY(g3,g3) = 0.4
    c: DistanceX(g8,g8) = 1
    c: DistanceY(g1,g1) = 4
    c: PointOnObject(g2,g6)
FEATURE [PartDesign::Revolution] Revolution007
  AddSubType = 0
  Angle = 360
  Axis = (0,0,1)
  Base = (0,0,0)
  ClaimChildren = false
  Fit = 0
  FitJoin = 0
  FixShape = 1
  InnerFit = 0
  InnerFitJoin = 0
  InvalidShape = false
  NewSolid = false
  Placement = pos=(0,0,0) rot=(1,0,0;1.5708rad)
  Profile = -> Sketch118
  ReferenceAxis = -> Sketch118 [V_Axis]
  Refine = true
  Suppress = false
  TreeRank = 0
  ValidateShape = true
  _ProfileBasedVersion = 0
FEATURE [PartDesign::Body] Body054  label="CoreMR148"
  AutoGroupSolids = false
  ClaimAllChildren = false
  ExportMode = 0
  FixShape = 1
  Group = -> [Sketch118,Revolution007]
  InvalidShape = false
  Origin = -> Origin162
  SingleSolid = true
  Tip = -> Revolution007
  TreeRank = 0
  ValidateShape = false
  _ExportChildren = -> [Revolution007]
  _GroupVersion = 1
FEATURE [Sketcher::SketchObject] Sketch119
  ArcFitTolerance = 0
  ExternalBSplineMaxDegree = 0
  ExternalBSplineTolerance = 0
  FixShape = 1
  FullyConstrained = true
  InternalTolerance = 1e-06
  InvalidShape = false
  MakeInternals = false
  MapMode = 5
  Placement = pos=(0,0,0) rot=(1,0,0;1.5708rad)
  TreeRank = 0
  ValidateShape = false
  sketch-geometry (4):
    g0: LineSegment StartX=-6 StartY=4 StartZ=0 EndX=-5 EndY=4 EndZ=0
    g1: LineSegment StartX=-5 StartY=4 StartZ=0 EndX=-5 EndY=0 EndZ=0
    g2: LineSegment StartX=-5 StartY=0 StartZ=0 EndX=-6 EndY=0 EndZ=0
    g3: LineSegment StartX=-6 StartY=0 StartZ=0 EndX=-6 EndY=4 EndZ=0
  constraints (12):
    c: Coincident(g0,g1)
    c: Coincident(g1,g2)
    c: Coincident(g2,g3)
    c: Coincident(g3,g0)
    c: Horizontal(g0)
    c: Horizontal(g2)
    c: Vertical(g1)
    c: Vertical(g3)
    c: PointOnObject(g1,g-1)
    c: DistanceY(g3,g3) = 4
    c: DistanceX(g1) = -5
    c: DistanceX(g2) = -6
FEATURE [PartDesign::Revolution] Revolution008
  AddSubType = 0
  Angle = 360
  Axis = (0,0,1)
  Base = (0,0,0)
  ClaimChildren = false
  Fit = 0
  FitJoin = 0
  FixShape = 1
  InnerFit = 0
  InnerFitJoin = 0
  InvalidShape = false
  NewSolid = false
  Placement = pos=(0,0,0) rot=(1,0,0;1.5708rad)
  Profile = -> Sketch119
  ReferenceAxis = -> Sketch119 [V_Axis]
  Refine = true
  Suppress = false
  TreeRank = 0
  ValidateShape = true
  _ProfileBasedVersion = 0
FEATURE [PartDesign::Body] Body055  label="Sleeve"
  AutoGroupSolids = false
  ClaimAllChildren = false
  ExportMode = 0
  FixShape = 1
  Group = -> [Sketch119,Revolution008]
  InvalidShape = false
  Origin = -> Origin082
  SingleSolid = true
  Tip = -> Revolution008
  TreeRank = 0
  ValidateShape = false
  _ExportChildren = -> [Revolution008]
  _GroupVersion = 1
